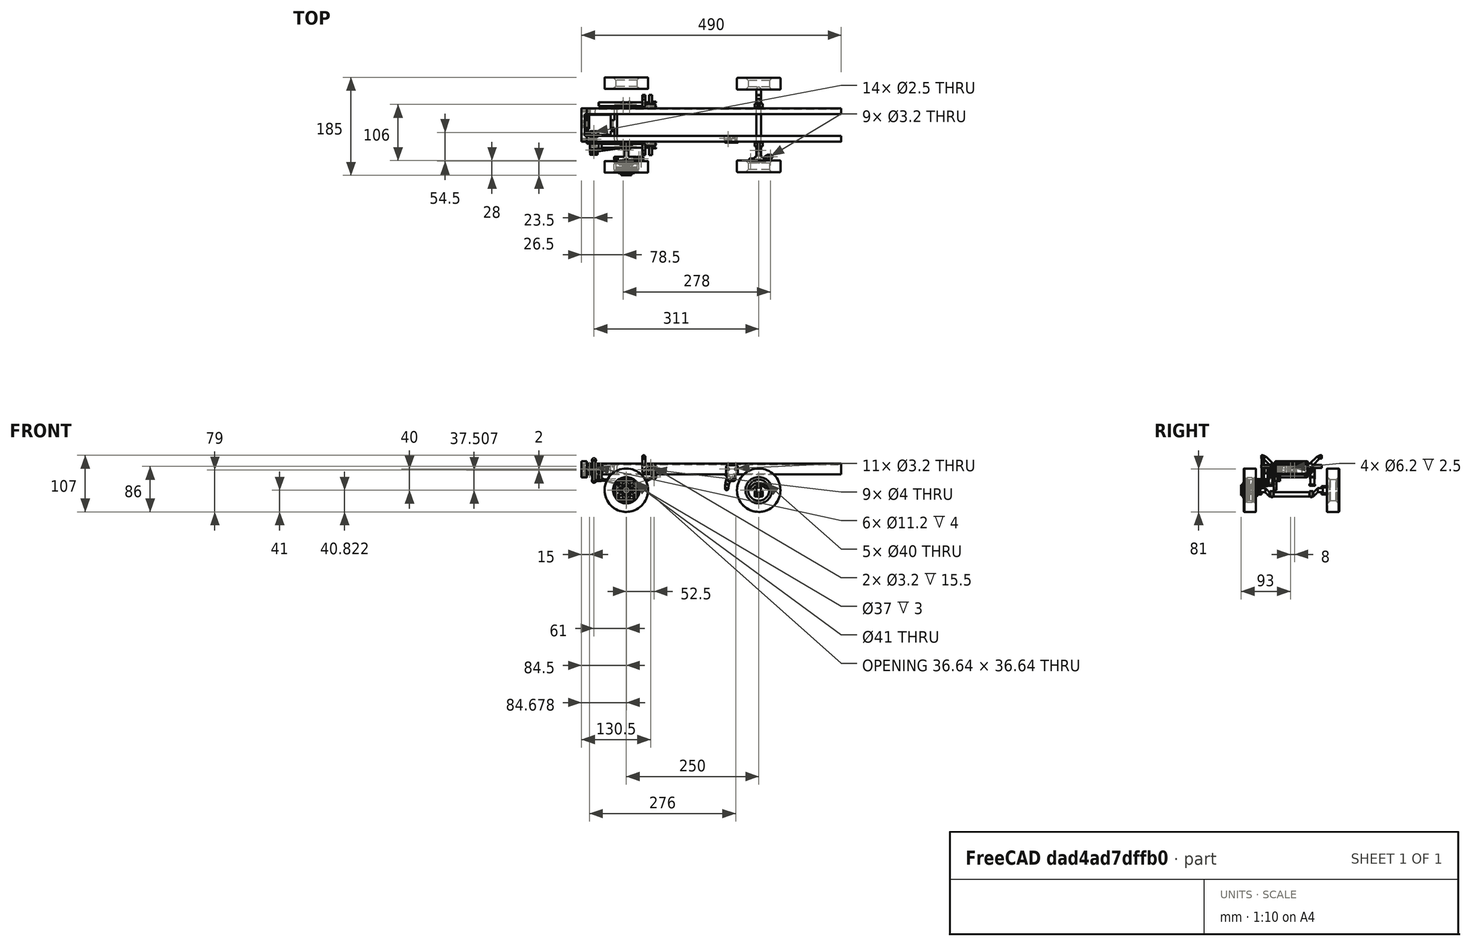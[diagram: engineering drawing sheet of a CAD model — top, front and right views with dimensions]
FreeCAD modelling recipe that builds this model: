
FCSTD DOCUMENT  (FreeCAD 0.16R6348 (Git))
Label: steering-linkage
License: All rights reserved
LicenseURL: http://en.wikipedia.org/wiki/All_rights_reserved
objects: Part::Cylinder×278, Part::Cut×158, Part::MultiFuse×147, Part::Box×113, Part::Fillet×39, Part::Chamfer×25, Part::Feature×10, Part::Mirroring×8, Part::Extrusion×5, App::DocumentObjectGroup×4, Part::Cone×3, Part::Loft×2
note: 788 computed .brp shape members not serialized (recipe doc carries the construction recipe); baked Part::Feature solids carry a one-line shape summary decoded from their .brp

FEATURE [Part::Box] Box416  label="Cube641"
  Height = 20
  Length = 480
  Placement = pos=(0,0,-92) rot=(0,0,1;0rad)
  Width = 11
FEATURE [Part::Box] Box417  label="Cube642"
  Height = 17
  Length = 480
  Placement = pos=(0,1.5,-90.5) rot=(0,0,1;0rad)
  Width = 10
FEATURE [Part::Cut] Cut429  label="Cut768"
  Base = -> Box416
  Tool = -> Box417
FEATURE [Part::Fillet] Fillet268
  Base = -> Cut429
  Edges = 2 edges r=3: [Edge11,Edge23]
  Placement = pos=(0,-1.5,0) rot=(0,0,1;0rad)
FEATURE [Part::Box] Box418  label="Cube643"
  Height = 20
  Length = 480
  Placement = pos=(0,0,-92) rot=(0,0,1;0rad)
  Width = 11
FEATURE [Part::Box] Box419  label="Cube644"
  Height = 17
  Length = 480
  Placement = pos=(0,1.5,-90.5) rot=(0,0,1;0rad)
  Width = 10
FEATURE [Part::Cut] Cut430  label="Cut769"
  Base = -> Box418
  Tool = -> Box419
FEATURE [Part::Fillet] Fillet269
  Base = -> Cut430
  Edges = 2 edges r=3: [Edge11,Edge23]
FEATURE [Part::Mirroring] Part__Mirroring036  label="Fillet269 (Mirror #29)"
  Base = (0,0,0)
  Normal = (0,1,0)
  Placement = pos=(0,61.5,0) rot=(0,0,1;0rad)
  Source = -> Fillet269
FEATURE [Part::MultiFuse] Fusion231  label="frame-00"
  Placement = pos=(23.5,55,71) rot=(0,0,1;0rad)
  Shapes = -> [Part__Mirroring036,Fillet268]
FEATURE [Part::MultiFuse] Fusion498
FEATURE [Part::Cut] Cut607
FEATURE [Part::Cut] Cut610  label="Cut880"
  Base = -> Cut607
FEATURE [Part::MultiFuse] Fusion500  label="central-axle"
  Shapes = -> [Cut610,Fusion498]
FEATURE [Part::Cylinder] Cylinder276
  Angle = 360
  Height = 22
  Placement = pos=(0,0,0) rot=(1,0,0;1.5708rad)
  Radius = 41
FEATURE [Part::Cylinder] Cylinder277
  Angle = 360
  Height = 22
  Placement = pos=(0,0,0) rot=(1,0,0;1.5708rad)
  Radius = 20
FEATURE [Part::Cut] Cut421  label="Cut764"
  Base = -> Cylinder276
  Tool = -> Cylinder277
FEATURE [Part::Fillet] Fillet260  label="wheel-000"
  Base = -> Cut421
  Edges = 2 edges r=1: [Edge1,Edge3]
  Placement = pos=(0,17,0) rot=(0,0,1;0rad)
FEATURE [Part::Cylinder] Cylinder278
  Angle = 360
  Height = 22
  Placement = pos=(0,0,0) rot=(1,0,0;1.5708rad)
  Radius = 41
FEATURE [Part::Cylinder] Cylinder279
  Angle = 360
  Height = 22
  Placement = pos=(0,0,0) rot=(1,0,0;1.5708rad)
  Radius = 20
FEATURE [Part::Cut] Cut422  label="Cut765"
  Base = -> Cylinder278
  Tool = -> Cylinder279
FEATURE [Part::Fillet] Fillet261  label="wheel-001"
  Base = -> Cut422
  Edges = 2 edges r=1: [Edge1,Edge3]
  Placement = pos=(0,175,0) rot=(0,0,1;0rad)
FEATURE [Part::Cylinder] Cylinder288
  Angle = 360
  Height = 22
  Placement = pos=(0,0,0) rot=(1,0,0;1.5708rad)
  Radius = 41
FEATURE [Part::Cylinder] Cylinder289
  Angle = 360
  Height = 22
  Placement = pos=(0,0,0) rot=(1,0,0;1.5708rad)
  Radius = 41
FEATURE [Part::Cylinder] Cylinder290
  Angle = 360
  Height = 22
  Placement = pos=(0,0,0) rot=(1,0,0;1.5708rad)
  Radius = 20
FEATURE [Part::Cut] Cut427  label="Cut766"
  Base = -> Cylinder289
  Tool = -> Cylinder290
FEATURE [Part::Fillet] Fillet267  label="wheel-007"
  Base = -> Cut427
  Edges = 2 edges r=1: [Edge1,Edge3]
  Placement = pos=(0,174,0) rot=(0,0,1;0rad)
FEATURE [Part::Cylinder] Cylinder291
  Angle = 360
  Height = 22
  Placement = pos=(0,0,0) rot=(1,0,0;1.5708rad)
  Radius = 20
FEATURE [Part::Cut] Cut428  label="Cut767"
  Base = -> Cylinder288
  Tool = -> Cylinder291
FEATURE [Part::Fillet] Fillet266  label="wheel-006"
  Base = -> Cut428
  Edges = 2 edges r=1: [Edge1,Edge3]
  Placement = pos=(0,18,0) rot=(0,0,1;0rad)
FEATURE [Part::MultiFuse] Fusion244
  Placement = pos=(348,0,-51) rot=(0,0,1;0rad)
  Shapes = -> [Fillet266,Fillet267]
FEATURE [Part::Chamfer] Chamfer056  label="whees-middle"
  Base = -> Fusion244
  Edges = 4 edges r=5: [Edge8,Edge9,Edge18,Edge19]
FEATURE [Part::MultiFuse] Fusion245
  Placement = pos=(98,0,-51) rot=(0,0,1;0rad)
  Shapes = -> [Fillet260,Fillet261]
FEATURE [Part::Chamfer] Chamfer057  label="whels-front"
  Base = -> Fusion245
  Edges = 4 edges r=5: [Edge8,Edge9,Edge18,Edge19]
FEATURE [Part::Cylinder] Cylinder640  label="Cylinder722"
  Angle = 360
  Height = 7
  Placement = pos=(60,105,0) rot=(0,0,1;4.18879rad)
  Radius = 105
FEATURE [Part::Cylinder] Cylinder641  label="Cylinder723"
  Angle = 360
  Height = 7
  Placement = pos=(60,105,0) rot=(0,0,1;4.10152rad)
  Radius = 103
FEATURE [Part::Cut] Cut109  label="leafspring-rear-left"
  Base = -> Cylinder640
  Placement = pos=(440,4,-64) rot=(1,0,0;1.5708rad)
  Tool = -> Cylinder641
FEATURE [Part::Cylinder] Cylinder642  label="Cylinder724"
  Angle = 360
  Height = 7
  Placement = pos=(60,105,0) rot=(0,0,1;4.18879rad)
  Radius = 105
FEATURE [Part::Cylinder] Cylinder643  label="Cylinder642"
  Angle = 360
  Height = 7
  Placement = pos=(60,105,0) rot=(0,0,1;4.10152rad)
  Radius = 103
FEATURE [Part::Cut] Cut110  label="leafspring-rear-right"
  Base = -> Cylinder642
  Placement = pos=(440,83,-64) rot=(1,0,0;1.5708rad)
  Tool = -> Cylinder643
FEATURE [Part::MultiFuse] Fusion091  label="leafsprings-front"
  Placement = pos=(-402,45,23) rot=(0,0,1;0rad)
  Shapes = -> [Cut109,Cut110]
FEATURE [Part::Cylinder] Cylinder654  label="Cylinder731"
  Angle = 360
  Height = 10
  Placement = pos=(0,0,12.7) rot=(1,0,0;1.5708rad)
  Radius = 2
FEATURE [Part::Cylinder] Cylinder655  label="Cylinder732"
  Angle = 360
  Height = 10
  Placement = pos=(0,0,0) rot=(1,0,0;1.5708rad)
  Radius = 2
FEATURE [Part::Box] Box439  label="Cube658"
  Height = 20
  Length = 8
  Placement = pos=(-4,-1,-3.5) rot=(0,0,1;0rad)
  Width = 1
FEATURE [Part::Fillet] Fillet320
  Base = -> Box439
  Edges = 4 edges r=2.99: [Edge2,Edge4,Edge6,Edge8]
FEATURE [Part::MultiFuse] Fusion437
  Shapes = -> [Cylinder654,Cylinder655]
FEATURE [Part::Cut] Cut559  label="Cut849"
  Base = -> Fillet320
  Placement = pos=(150,42,-27) rot=(0,-1,0;0.174533rad)
  Tool = -> Fusion437
FEATURE [Part::Cylinder] Cylinder656  label="Cylinder733"
  Angle = 360
  Height = 10
  Placement = pos=(0,0,12.7) rot=(1,0,0;1.5708rad)
  Radius = 2
FEATURE [Part::Cylinder] Cylinder657  label="Cylinder734"
  Angle = 360
  Height = 10
  Placement = pos=(0,0,0) rot=(1,0,0;1.5708rad)
  Radius = 2
FEATURE [Part::MultiFuse] Fusion438
  Shapes = -> [Cylinder656,Cylinder657]
FEATURE [Part::Box] Box440  label="Cube659"
  Height = 20
  Length = 8
  Placement = pos=(-4,-1,-3.5) rot=(0,0,1;0rad)
  Width = 1
FEATURE [Part::Fillet] Fillet321
  Base = -> Box440
  Edges = 4 edges r=2.99: [Edge2,Edge4,Edge6,Edge8]
FEATURE [Part::Cut] Cut560  label="Cut850"
  Base = -> Fillet321
  Placement = pos=(150,50,-27) rot=(0,-1,0;0.174533rad)
  Tool = -> Fusion438
FEATURE [Part::MultiFuse] Fusion439  label="leafspring-bisquits-front-left"
  Placement = pos=(0.5,0,1) rot=(0,0,1;0rad)
  Shapes = -> [Cut559,Cut560]
FEATURE [Part::Cylinder] Cylinder658  label="Cylinder768"
  Angle = 360
  Height = 10
  Placement = pos=(0,0,12.7) rot=(1,0,0;1.5708rad)
  Radius = 2
FEATURE [Part::Cylinder] Cylinder659  label="Cylinder712"
  Angle = 360
  Height = 10
  Placement = pos=(0,0,0) rot=(1,0,0;1.5708rad)
  Radius = 2
FEATURE [Part::Box] Box441  label="Cube660"
  Height = 20
  Length = 8
  Placement = pos=(-4,-1,-3.5) rot=(0,0,1;0rad)
  Width = 1
FEATURE [Part::Fillet] Fillet322
  Base = -> Box441
  Edges = 4 edges r=2.99: [Edge2,Edge4,Edge6,Edge8]
FEATURE [Part::MultiFuse] Fusion441
  Shapes = -> [Cylinder658,Cylinder659]
FEATURE [Part::Cut] Cut561  label="Cut851"
  Base = -> Fillet322
  Placement = pos=(150,42,-27) rot=(0,-1,0;0.174533rad)
  Tool = -> Fusion441
FEATURE [Part::Cylinder] Cylinder660  label="Cylinder783"
  Angle = 360
  Height = 10
  Placement = pos=(0,0,12.7) rot=(1,0,0;1.5708rad)
  Radius = 2
FEATURE [Part::Cylinder] Cylinder661  label="Cylinder784"
  Angle = 360
  Height = 10
  Placement = pos=(0,0,0) rot=(1,0,0;1.5708rad)
  Radius = 2
FEATURE [Part::MultiFuse] Fusion442
  Shapes = -> [Cylinder660,Cylinder661]
FEATURE [Part::Box] Box442  label="Cube661"
  Height = 20
  Length = 8
  Placement = pos=(-4,-1,-3.5) rot=(0,0,1;0rad)
  Width = 1
FEATURE [Part::Fillet] Fillet323
  Base = -> Box442
  Edges = 4 edges r=2.99: [Edge2,Edge4,Edge6,Edge8]
FEATURE [Part::Cut] Cut562  label="Cut852"
  Base = -> Fillet323
  Placement = pos=(150,50,-27) rot=(0,-1,0;0.174533rad)
  Tool = -> Fusion442
FEATURE [Part::MultiFuse] Fusion440  label="leafspring-bisquits-front-right"
  Placement = pos=(0.5,79,1) rot=(0,0,1;0rad)
  Shapes = -> [Cut561,Cut562]
FEATURE [Part::Cylinder] Cylinder681  label="Cylinder798"
  Angle = 360
  Height = 4
  Radius = 4.5
FEATURE [Part::Cylinder] Cylinder001
  Angle = 360
  Height = 4
  Placement = pos=(12,0,0) rot=(0,0,1;0rad)
  Radius = 4.5
FEATURE [Part::Box] Box453
  Height = 1
  Length = 12
  Placement = pos=(0,-4,0) rot=(0,0,1;0rad)
  Width = 8
FEATURE [Part::MultiFuse] Fusion453
  Shapes = -> [Box453,Cylinder001,Cylinder681]
FEATURE [Part::Box] Box454
  Height = 4
  Length = 12
  Placement = pos=(0,-4,0) rot=(0,0,1;0rad)
  Width = 1
FEATURE [Part::Box] Box455
  Height = 4
  Length = 12
  Placement = pos=(0,3,0) rot=(0,0,1;0rad)
  Width = 1
FEATURE [Part::Box] Box456
  Height = 1
  Length = 12
  Placement = pos=(0,3.5,3) rot=(0,0,1;0rad)
  Width = 0.5
FEATURE [Part::MultiFuse] Fusion001
  Shapes = -> [Fusion453,Box455,Box454]
FEATURE [Part::Box] Box004
  Height = 1
  Length = 12
  Placement = pos=(0,-4,3) rot=(0,0,1;0rad)
  Width = 0.5
FEATURE [Part::MultiFuse] Fusion002
  Shapes = -> [Fusion001,Box456,Box004]
FEATURE [Part::Cylinder] Cylinder002
  Angle = 360
  Height = 4
  Radius = 1.5
FEATURE [Part::Box] Box005
  Height = 10
  Length = 10
  Placement = pos=(-5,0,0) rot=(0,0,1;0rad)
  Width = 10
FEATURE [Part::Cut] Cut571  label="Cut859"
  Base = -> Cylinder002
  Placement = pos=(0,-4,0) rot=(0,0,1;0rad)
  Tool = -> Box005
FEATURE [Part::Cylinder] Cylinder003
  Angle = 360
  Height = 4
  Radius = 1.5
FEATURE [Part::Box] Box006
  Height = 10
  Length = 10
  Placement = pos=(-5,0,0) rot=(0,0,1;0rad)
  Width = 10
FEATURE [Part::Cut] Cut572  label="Cut860"
  Base = -> Cylinder003
  Placement = pos=(12,-4,0) rot=(0,0,1;0rad)
  Tool = -> Box006
FEATURE [Part::Cylinder] Cylinder682  label="Cylinder799"
  Angle = 360
  Height = 4
  Radius = 1.5
FEATURE [Part::Box] Box007
  Height = 10
  Length = 10
  Placement = pos=(-5,0,0) rot=(0,0,1;0rad)
  Width = 10
FEATURE [Part::Cut] Cut002
  Base = -> Cylinder682
  Placement = pos=(0,4,0) rot=(0,0,1;3.14159rad)
  Tool = -> Box007
FEATURE [Part::Cylinder] Cylinder005
  Angle = 360
  Height = 4
  Radius = 1.5
FEATURE [Part::Box] Box008
  Height = 10
  Length = 10
  Placement = pos=(-5,0,0) rot=(0,0,1;0rad)
  Width = 10
FEATURE [Part::Cut] Cut003
  Base = -> Cylinder005
  Placement = pos=(12,4,0) rot=(0,0,1;3.14159rad)
  Tool = -> Box008
FEATURE [Part::MultiFuse] Fusion003
  Shapes = -> [Fusion002,Cut003,Cut002,Cut572,Cut571]
FEATURE [Part::Cylinder] Cylinder006
  Angle = 360
  Height = 10
  Radius = 1.6
FEATURE [Part::Cylinder] Cylinder007
  Angle = 360
  Height = 10
  Placement = pos=(12,0,0) rot=(0,0,1;0rad)
  Radius = 1.6
FEATURE [Part::MultiFuse] Fusion004
  Shapes = -> [Cylinder007,Cylinder006]
FEATURE [Part::Cut] Cut004
  Base = -> Fusion003
  Tool = -> Fusion004
FEATURE [Part::Cylinder] Cylinder008
  Angle = 360
  Height = 7
  Placement = pos=(6,3.5,153) rot=(1,0,0;1.5708rad)
  Radius = 150
FEATURE [Part::Cut] Cut005
  Base = -> Cut004
  Tool = -> Cylinder008
FEATURE [Part::Box] Box457
  Height = 3
  Length = 6
  Placement = pos=(3,-3.5,1) rot=(0,0,1;0rad)
  Width = 7
FEATURE [Part::Cut] Cut006
  Base = -> Cut005
  Tool = -> Box457
FEATURE [Part::Box] Box015
  Height = 1.5
  Length = 26
  Placement = pos=(-6,-6,0) rot=(0,0,1;0rad)
  Width = 13
FEATURE [Part::Cut] Cut012
  Base = -> Cut006
  Placement = pos=(0,0,-1.5) rot=(0,0,1;0rad)
  Tool = -> Box015
FEATURE [Part::Box] Box016
  Height = 1
  Length = 8
  Placement = pos=(2,-4,0) rot=(0,0,1;0rad)
  Width = 8
FEATURE [Part::MultiFuse] Fusion008  label="leafspring-spacer-front-left"
  Placement = pos=(92,45,-42.5) rot=(0,0,1;0rad)
  Shapes = -> [Cut012,Box016]
FEATURE [Part::Cylinder] Cylinder683  label="Cylinder800"
  Angle = 360
  Height = 4
  Radius = 4.5
FEATURE [Part::Cylinder] Cylinder684  label="Cylinder801"
  Angle = 360
  Height = 4
  Placement = pos=(12,0,0) rot=(0,0,1;0rad)
  Radius = 4.5
FEATURE [Part::Box] Box458
  Height = 1
  Length = 12
  Placement = pos=(0,-4,0) rot=(0,0,1;0rad)
  Width = 8
FEATURE [Part::MultiFuse] Fusion454
  Shapes = -> [Box458,Cylinder684,Cylinder683]
FEATURE [Part::Box] Box459
  Height = 4
  Length = 12
  Placement = pos=(0,-4,0) rot=(0,0,1;0rad)
  Width = 1
FEATURE [Part::Box] Box460
  Height = 4
  Length = 12
  Placement = pos=(0,3,0) rot=(0,0,1;0rad)
  Width = 1
FEATURE [Part::Box] Box461
  Height = 1
  Length = 12
  Placement = pos=(0,3.5,3) rot=(0,0,1;0rad)
  Width = 0.5
FEATURE [Part::MultiFuse] Fusion455
  Shapes = -> [Fusion454,Box460,Box459]
FEATURE [Part::Box] Box462
  Height = 1
  Length = 12
  Placement = pos=(0,-4,3) rot=(0,0,1;0rad)
  Width = 0.5
FEATURE [Part::MultiFuse] Fusion456
  Shapes = -> [Fusion455,Box461,Box462]
FEATURE [Part::Cylinder] Cylinder685  label="Cylinder802"
  Angle = 360
  Height = 4
  Radius = 1.5
FEATURE [Part::Box] Box463
  Height = 10
  Length = 10
  Placement = pos=(-5,0,0) rot=(0,0,1;0rad)
  Width = 10
FEATURE [Part::Cut] Cut573  label="Cut861"
  Base = -> Cylinder685
  Placement = pos=(0,-4,0) rot=(0,0,1;0rad)
  Tool = -> Box463
FEATURE [Part::Cylinder] Cylinder686  label="Cylinder879"
  Angle = 360
  Height = 4
  Radius = 1.5
FEATURE [Part::Box] Box464
  Height = 10
  Length = 10
  Placement = pos=(-5,0,0) rot=(0,0,1;0rad)
  Width = 10
FEATURE [Part::Cut] Cut574  label="Cut862"
  Base = -> Cylinder686
  Placement = pos=(12,-4,0) rot=(0,0,1;0rad)
  Tool = -> Box464
FEATURE [Part::Cylinder] Cylinder687  label="Cylinder804"
  Angle = 360
  Height = 4
  Radius = 1.5
FEATURE [Part::Box] Box465
  Height = 10
  Length = 10
  Placement = pos=(-5,0,0) rot=(0,0,1;0rad)
  Width = 10
FEATURE [Part::Cut] Cut575  label="Cut863"
  Base = -> Cylinder687
  Placement = pos=(0,4,0) rot=(0,0,1;3.14159rad)
  Tool = -> Box465
FEATURE [Part::Cylinder] Cylinder688  label="Cylinder865"
  Angle = 360
  Height = 4
  Radius = 1.5
FEATURE [Part::Box] Box466
  Height = 10
  Length = 10
  Placement = pos=(-5,0,0) rot=(0,0,1;0rad)
  Width = 10
FEATURE [Part::Cut] Cut576  label="Cut864"
  Base = -> Cylinder688
  Placement = pos=(12,4,0) rot=(0,0,1;3.14159rad)
  Tool = -> Box466
FEATURE [Part::MultiFuse] Fusion457
  Shapes = -> [Fusion456,Cut576,Cut575,Cut574,Cut573]
FEATURE [Part::Cylinder] Cylinder689  label="Cylinder908"
  Angle = 360
  Height = 10
  Radius = 1.6
FEATURE [Part::Cylinder] Cylinder690  label="Cylinder909"
  Angle = 360
  Height = 10
  Placement = pos=(12,0,0) rot=(0,0,1;0rad)
  Radius = 1.6
FEATURE [Part::MultiFuse] Fusion458
  Shapes = -> [Cylinder690,Cylinder689]
FEATURE [Part::Cut] Cut577  label="Cut865"
  Base = -> Fusion457
  Tool = -> Fusion458
FEATURE [Part::Cylinder] Cylinder691  label="Cylinder910"
  Angle = 360
  Height = 7
  Placement = pos=(6,3.5,153) rot=(1,0,0;1.5708rad)
  Radius = 150
FEATURE [Part::Cut] Cut578  label="Cut866"
  Base = -> Cut577
  Tool = -> Cylinder691
FEATURE [Part::Box] Box467
  Height = 3
  Length = 6
  Placement = pos=(3,-3.5,1) rot=(0,0,1;0rad)
  Width = 7
FEATURE [Part::Cut] Cut579  label="Cut867"
  Base = -> Cut578
  Tool = -> Box467
FEATURE [Part::Box] Box468
  Height = 1.5
  Length = 26
  Placement = pos=(-6,-6,0) rot=(0,0,1;0rad)
  Width = 13
FEATURE [Part::Cut] Cut580  label="Cut868"
  Base = -> Cut579
  Placement = pos=(0,0,-1.5) rot=(0,0,1;0rad)
  Tool = -> Box468
FEATURE [Part::Box] Box469
  Height = 1
  Length = 8
  Placement = pos=(2,-4,0) rot=(0,0,1;0rad)
  Width = 8
FEATURE [Part::MultiFuse] Fusion459  label="leafspring-spacer-front-right"
  Placement = pos=(92,124,-42.5) rot=(0,0,1;0rad)
  Shapes = -> [Cut580,Box469]
FEATURE [Part::Box] Box021
  Height = 1
  Length = 12
  Placement = pos=(0,-21.75,0) rot=(0,0,1;0rad)
  Width = 7.5
FEATURE [Part::Cylinder] Cylinder016
  Angle = 360
  Height = 1
  Placement = pos=(12,-18,0) rot=(0,0,1;0rad)
  Radius = 4.75
FEATURE [Part::Cylinder] Cylinder017
  Angle = 360
  Height = 1
  Placement = pos=(0,-18,0) rot=(0,0,1;0rad)
  Radius = 4.75
FEATURE [Part::Box] Box022
  Height = 300
  Length = 317
  Placement = pos=(-150,-22,0) rot=(0,0,1;0rad)
  Width = 10
FEATURE [Part::Cylinder] Cylinder018
  Angle = 360
  Height = 7.5
  Placement = pos=(6,-14.25,49.2) rot=(1,0,0;1.5708rad)
  Radius = 50
FEATURE [Part::Cut] Cut018
  Base = -> Cylinder018
  Tool = -> Box022
FEATURE [Part::MultiFuse] Fusion014
  Shapes = -> [Box021,Cut018,Cylinder017,Cylinder016]
FEATURE [Part::Cylinder] Cylinder019
  Angle = 360
  Height = 7.5
  Placement = pos=(6,-14.25,49.2) rot=(1,0,0;1.5708rad)
  Radius = 51
FEATURE [Part::Cylinder] Cylinder020
  Angle = 360
  Height = 7.5
  Placement = pos=(6,-14.25,49.2) rot=(1,0,0;1.5708rad)
  Radius = 50
FEATURE [Part::Cut] Cut019
  Base = -> Cylinder019
  Tool = -> Cylinder020
FEATURE [Part::Cut] Cut020
  Base = -> Fusion014
  Tool = -> Cut019
FEATURE [Part::Cylinder] Cylinder021
  Angle = 360
  Height = 10
  Placement = pos=(12,-18,-9.2) rot=(0,0,1;0rad)
  Radius = 1.6
FEATURE [Part::Cylinder] Cylinder022
  Angle = 360
  Height = 10
  Placement = pos=(0,-18,-9.2) rot=(0,0,1;0rad)
  Radius = 1.6
FEATURE [Part::MultiFuse] Fusion015
  Placement = pos=(0,0,5) rot=(0,0,1;0rad)
  Shapes = -> [Cylinder021,Cylinder022]
FEATURE [Part::Cut] Cut021  label="leafspring-spacer-upper-front-left"
  Base = -> Cut020
  Placement = pos=(92,63,-38) rot=(0,0,1;0rad)
  Tool = -> Fusion015
FEATURE [Part::Box] Box485  label="Cube687"
  Height = 17
  Length = 25
  Placement = pos=(128,45.5,-18) rot=(0,0,1;0rad)
  Width = 8
FEATURE [Part::Cylinder] Cylinder735  label="Cylinder911"
  Angle = 360
  Height = 25.5
  Placement = pos=(144,53.5,-6) rot=(1,0,0;1.5708rad)
  Radius = 3
FEATURE [Part::Cylinder] Cylinder736  label="Cylinder912"
  Angle = 360
  Height = 23
  Placement = pos=(131,51,-6) rot=(1,0,0;0.785398rad)
  Radius = 3
FEATURE [Part::Feature] Face036
  shape: bbox 7.785 x 2e-07 x 7.712 mm, 1 faces, 0 solids (baked)
FEATURE [Part::Feature] Face037
  shape: bbox 7.318 x 4.987 x 4.987 mm, 1 faces, 0 solids (baked)
FEATURE [Part::Loft] Loft014
  Closed = false
  Ruled = true
  Sections = -> [Face036,Face037]
  Solid = true
FEATURE [Part::Cylinder] Cylinder737  label="Cylinder902"
  Angle = 360
  Height = 3
  Placement = pos=(131,31,12) rot=(1,0,0;1.5708rad)
  Radius = 3
FEATURE [Part::MultiFuse] Fusion480
  Shapes = -> [Loft014,Cylinder737]
FEATURE [Part::Cylinder] Cylinder738  label="Cylinder913"
  Angle = 360
  Height = 5
  Placement = pos=(131,33,12) rot=(1,0,0;1.5708rad)
  Radius = 1.6
FEATURE [Part::Cylinder] Cylinder739  label="Cylinder914"
  Angle = 360
  Height = 15.5
  Placement = pos=(144,43.5,-6) rot=(1,0,0;1.5708rad)
  Radius = 1.6
FEATURE [Part::MultiFuse] Fusion481
  Shapes = -> [Cylinder738,Cylinder739]
FEATURE [Part::Cylinder] Cylinder740  label="Cylinder915"
  Angle = 360
  Height = 15
  Placement = pos=(132,61.5,-16) rot=(1,0,0;1.5708rad)
  Radius = 1.6
FEATURE [Part::Cylinder] Cylinder741  label="Cylinder916"
  Angle = 360
  Height = 2.5
  Placement = pos=(132,49,-16) rot=(1,0,0;1.5708rad)
  Radius = 3
FEATURE [Part::MultiFuse] Fusion482
  Placement = pos=(4,-1.5,4) rot=(0,0,1;0rad)
  Shapes = -> [Cylinder740,Cylinder741]
FEATURE [Part::Box] Box488  label="Cube690"
  Height = 9.5
  Length = 10
  Placement = pos=(143,45.5,-18) rot=(0,0,1;0rad)
  Width = 5
FEATURE [Part::Fillet] Fillet337
  Base = -> Box488
  Edges = 1 edges r=4: [Edge2]
FEATURE [Part::Cylinder] Cylinder745  label="Cylinder890"
  Angle = 360
  Height = 3.5
  Placement = pos=(148.5,53.5,-13.5) rot=(1,0,0;1.5708rad)
  Radius = 3
FEATURE [Part::Cylinder] Cylinder746  label="Cylinder917"
  Angle = 360
  Height = 1.75
  Placement = pos=(498.5,51.75,-13.5) rot=(1,0,0;1.5708rad)
  Radius = 2.1
FEATURE [Part::Cylinder] Cylinder747  label="Cylinder892"
  Angle = 360
  Height = 3.5
  Placement = pos=(498.5,53.5,-13.5) rot=(1,0,0;1.5708rad)
  Radius = 1.5
FEATURE [Part::MultiFuse] Fusion484
  Placement = pos=(-350,0,0) rot=(0,0,1;0rad)
  Shapes = -> [Cylinder746,Cylinder747]
FEATURE [Part::Cylinder] Cylinder748  label="Cylinder964"
  Angle = 360
  Height = 75
  Placement = pos=(121,50,-7) rot=(0,1,0;1.5708rad)
  Radius = 3
FEATURE [Part::Cut] Cut595  label="Cut874"
  Base = -> Box485
  Tool = -> Fillet337
FEATURE [Part::MultiFuse] Fusion485
  Shapes = -> [Cut595,Cylinder745]
FEATURE [Part::Cut] Cut596  label="Cut875"
  Base = -> Fusion485
  Tool = -> Fusion484
FEATURE [Part::MultiFuse] Fusion486
  Shapes = -> [Cut596,Fusion480,Cylinder736,Cylinder735]
FEATURE [Part::Cut] Cut597
  Base = -> Fusion486
  Tool = -> Fusion481
FEATURE [Part::Cut] Cut598  label="wing-support-left_"
  Base = -> Cut597
  Tool = -> Fusion482
FEATURE [Part::Box] Box489  label="Cube691"
  Height = 17
  Length = 25
  Placement = pos=(128,45.5,-18) rot=(0,0,1;0rad)
  Width = 8
FEATURE [Part::Cylinder] Cylinder749  label="Cylinder965"
  Angle = 360
  Height = 25.5
  Placement = pos=(144,53.5,-6) rot=(1,0,0;1.5708rad)
  Radius = 3
FEATURE [Part::Cylinder] Cylinder750  label="Cylinder966"
  Angle = 360
  Height = 23
  Placement = pos=(131,51,-6) rot=(1,0,0;0.785398rad)
  Radius = 3
FEATURE [Part::Feature] Face038
  shape: bbox 7.785 x 2e-07 x 7.712 mm, 1 faces, 0 solids (baked)
FEATURE [Part::Feature] Face039
  shape: bbox 7.318 x 4.987 x 4.987 mm, 1 faces, 0 solids (baked)
FEATURE [Part::Loft] Loft015
  Closed = false
  Ruled = true
  Sections = -> [Face038,Face039]
  Solid = true
FEATURE [Part::Cylinder] Cylinder751  label="Cylinder967"
  Angle = 360
  Height = 3
  Placement = pos=(131,31,12) rot=(1,0,0;1.5708rad)
  Radius = 3
FEATURE [Part::MultiFuse] Fusion487
  Shapes = -> [Loft015,Cylinder751]
FEATURE [Part::Cylinder] Cylinder752  label="Cylinder968"
  Angle = 360
  Height = 5
  Placement = pos=(131,33,12) rot=(1,0,0;1.5708rad)
  Radius = 1.6
FEATURE [Part::Cylinder] Cylinder753  label="Cylinder969"
  Angle = 360
  Height = 15.5
  Placement = pos=(144,43.5,-6) rot=(1,0,0;1.5708rad)
  Radius = 1.6
FEATURE [Part::MultiFuse] Fusion488
  Shapes = -> [Cylinder752,Cylinder753]
FEATURE [Part::Cylinder] Cylinder754  label="Cylinder970"
  Angle = 360
  Height = 15
  Placement = pos=(132,61.5,-16) rot=(1,0,0;1.5708rad)
  Radius = 1.6
FEATURE [Part::Cylinder] Cylinder755  label="Cylinder971"
  Angle = 360
  Height = 2.5
  Placement = pos=(132,49,-16) rot=(1,0,0;1.5708rad)
  Radius = 3
FEATURE [Part::MultiFuse] Fusion489
  Placement = pos=(4,-1.5,4) rot=(0,0,1;0rad)
  Shapes = -> [Cylinder754,Cylinder755]
FEATURE [Part::Box] Box490  label="Cube692"
  Height = 9.5
  Length = 10
  Placement = pos=(143,45.5,-18) rot=(0,0,1;0rad)
  Width = 5
FEATURE [Part::Fillet] Fillet338
  Base = -> Box490
  Edges = 1 edges r=4: [Edge2]
FEATURE [Part::Cylinder] Cylinder756  label="Cylinder972"
  Angle = 360
  Height = 3.5
  Placement = pos=(148.5,53.5,-13.5) rot=(1,0,0;1.5708rad)
  Radius = 3
FEATURE [Part::Cylinder] Cylinder757  label="Cylinder973"
  Angle = 360
  Height = 1.75
  Placement = pos=(498.5,51.75,-13.5) rot=(1,0,0;1.5708rad)
  Radius = 2.1
FEATURE [Part::Cylinder] Cylinder758  label="Cylinder941"
  Angle = 360
  Height = 3.5
  Placement = pos=(498.5,53.5,-13.5) rot=(1,0,0;1.5708rad)
  Radius = 1.5
FEATURE [Part::MultiFuse] Fusion490
  Placement = pos=(-350,0,0) rot=(0,0,1;0rad)
  Shapes = -> [Cylinder757,Cylinder758]
FEATURE [Part::Cut] Cut602  label="Cut877"
  Base = -> Box489
  Tool = -> Fillet338
FEATURE [Part::MultiFuse] Fusion492
  Shapes = -> [Cut602,Cylinder756]
FEATURE [Part::Cut] Cut600  label="Cut876"
  Base = -> Fusion492
  Tool = -> Fusion490
FEATURE [Part::MultiFuse] Fusion491
  Shapes = -> [Cut600,Fusion487,Cylinder750,Cylinder749]
FEATURE [Part::Cut] Cut601
  Base = -> Fusion491
  Tool = -> Fusion488
FEATURE [Part::Cut] Cut599  label="wing-support-left001"
  Base = -> Cut601
  Tool = -> Fusion489
FEATURE [Part::Mirroring] Part__Mirroring095  label="wing-support-right"
  Base = (0,0,0)
  Normal = (0,1,0)
  Placement = pos=(0,170,0) rot=(0,0,1;0rad)
  Source = -> Cut599
FEATURE [Part::Cut] Cut603  label="wing-support-left"
  Base = -> Cut598
  Tool = -> Cylinder748
FEATURE [Part::Cylinder] Cylinder692  label="Cylinder942"
  Angle = 360
  Height = 10
  Placement = pos=(3,60,10) rot=(1,0,0;1.5708rad)
  Radius = 1.2
FEATURE [Part::Cylinder] Cylinder693  label="Cylinder943"
  Angle = 360
  Height = 10
  Placement = pos=(3,10,10) rot=(1,0,0;1.5708rad)
  Radius = 1.2
FEATURE [Part::Box] Box472  label="Cube674"
  Height = 17
  Length = 16
  Placement = pos=(-2,0,1.5) rot=(0,0,1;0rad)
  Width = 60
FEATURE [Part::Box] Box473  label="Cube675"
  Height = 25.5
  Length = 10
  Placement = pos=(-12,0,-5) rot=(0,0,1;0rad)
  Width = 63
FEATURE [Part::Cylinder] Cylinder694  label="Cylinder944"
  Angle = 360
  Height = 11
  Placement = pos=(-2,66.5,-1) rot=(0,1,0;1.5708rad)
  Radius = 1.25
FEATURE [Part::Cylinder] Cylinder695  label="Cylinder974"
  Angle = 360
  Height = 11
  Placement = pos=(-2,13.5,-1) rot=(0,1,0;1.5708rad)
  Radius = 1.25
FEATURE [Part::Cylinder] Cylinder696  label="Cylinder975"
  Angle = 360
  Height = 15
  Placement = pos=(-2,57,15) rot=(0,1,0;1.5708rad)
  Radius = 1.25
FEATURE [Part::Cylinder] Cylinder697  label="Cylinder976"
  Angle = 360
  Height = 15
  Placement = pos=(-2,23,15) rot=(0,1,0;1.5708rad)
  Radius = 1.25
FEATURE [Part::MultiFuse] Fusion460
  Placement = pos=(-10,-10,1) rot=(0,0,1;0rad)
  Shapes = -> [Cylinder694,Cylinder697,Cylinder695,Cylinder696]
FEATURE [Part::Fillet] Fillet332
  Base = -> Box473
  Edges = 4 edges r=3: [Edge9,Edge10,Edge11,Edge12]
  Placement = pos=(25.5,53.5,-21.5) rot=(0,0,1;0rad)
FEATURE [Part::Fillet] Fillet333
  Base = -> Box472
  Edges = 4 edges r=3: [Edge9,Edge10,Edge11,Edge12]
  Placement = pos=(25.5,55,-21) rot=(0,0,1;0rad)
FEATURE [Part::MultiFuse] Fusion462
  Placement = pos=(0,0,2) rot=(0,0,1;0rad)
  Shapes = -> [Cylinder692,Cylinder693]
FEATURE [Part::MultiFuse] Fusion463
  Placement = pos=(25.5,55,-23) rot=(0,0,1;0rad)
  Shapes = -> [Fusion460,Fusion462]
FEATURE [Part::MultiFuse] Fusion464
  Shapes = -> [Fillet332,Fillet333]
FEATURE [Part::Cut] Cut581  label="cross-member-front_00"
  Base = -> Fusion464
  Tool = -> Fusion463
FEATURE [Part::Cylinder] Cylinder770  label="Cylinder977"
  Angle = 360
  Height = 3
  Placement = pos=(0,0,1) rot=(0,0,1;0rad)
  Radius = 4
FEATURE [Part::Cylinder] Cylinder771  label="Cylinder978"
  Angle = 360
  Height = 3
  Placement = pos=(-37,7,3) rot=(0,0,1;0rad)
  Radius = 4
FEATURE [Part::Cylinder] Cylinder772  label="Cylinder979"
  Angle = 360
  Height = 4
  Placement = pos=(-15,0,8) rot=(0,0,1;0rad)
  Radius = 4.5
FEATURE [Part::Box] Box507  label="Cube021"
  Height = 4
  Length = 8
  Placement = pos=(-19,0,8) rot=(0,0,1;0rad)
  Width = 27
FEATURE [Part::Cylinder] Cylinder773  label="Cylinder980"
  Angle = 360
  Height = 4
  Placement = pos=(-15,27,8) rot=(0,0,1;0rad)
  Radius = 4
FEATURE [Part::Cylinder] Cylinder774  label="Cylinder981"
  Angle = 360
  Height = 2
  Placement = pos=(-15,0,8) rot=(0,0,1;0rad)
  Radius = 3.2
FEATURE [Part::Box] Box508  label="Cube022"
  Height = 4
  Length = 11
  Placement = pos=(-15,-4,8) rot=(0,0,1;0rad)
  Width = 8
FEATURE [Part::Box] Box023  label="Cube023"
  Height = 4
  Length = 6
  Placement = pos=(-37,3,8) rot=(0,0,1;0rad)
  Width = 8
FEATURE [Part::Box] Box024  label="Cube709"
  Height = 4
  Length = 15
  Placement = pos=(-36,5,8) rot=(0,0,-1;0.663225rad)
  Width = 8
FEATURE [Part::Box] Box025  label="Cube025"
  Height = 4
  Length = 9
  Placement = pos=(-24,-4,8) rot=(0,0,1;0rad)
  Width = 8
FEATURE [Part::Box] Box026  label="Cube026"
  Height = 4
  Length = 10
  Placement = pos=(-30,-14,8) rot=(0,0,1;0rad)
  Width = 10
FEATURE [Part::Box] Box027  label="Cube027"
  Height = 4
  Length = 10
  Placement = pos=(-35,11,8) rot=(0,0,1;0rad)
  Width = 10
FEATURE [Part::MultiFuse] Fusion507
  Shapes = -> [Box026,Box027]
FEATURE [Part::MultiFuse] Fusion017
  Shapes = -> [Box023,Box024,Box025]
FEATURE [Part::Cut] Cut609  label="Cut881"
  Base = -> Fusion017
  Tool = -> Fusion507
FEATURE [Part::Cylinder] Cylinder775  label="Cylinder982"
  Angle = 360
  Height = 10
  Radius = 1.6
FEATURE [Part::Cylinder] Cylinder776  label="Cylinder983"
  Angle = 360
  Height = 10
  Placement = pos=(-37,7,2) rot=(0,0,1;0rad)
  Radius = 1.6
FEATURE [Part::Box] Box028  label="Cube028"
  Height = 4
  Length = 14
  Placement = pos=(-15,-6,8) rot=(0,0,1;0.785398rad)
  Width = 14
FEATURE [Part::Box] Box029  label="Cube029"
  Height = 4
  Length = 10
  Placement = pos=(-20,-14,8) rot=(0,0,1;0rad)
  Width = 10
FEATURE [Part::Cut] Cut013
  Base = -> Box028
  Tool = -> Box029
FEATURE [Part::MultiFuse] Fusion508
  Shapes = -> [Box508,Box507,Cut013,Cut609,Cylinder773,Cylinder772]
FEATURE [Part::Cut] Cut014
  Base = -> Fusion508
  Tool = -> Cylinder774
FEATURE [Part::Box] Box032  label="Cube032"
  Height = 11
  Length = 10
  Placement = pos=(-10,-4,1) rot=(0,0,1;0rad)
  Width = 8
FEATURE [Part::Chamfer] Chamfer082
  Base = -> Box032
  Edges = 1 edges r=7: [Edge4]
FEATURE [Part::Chamfer] Chamfer083
  Base = -> Chamfer082
  Edges = 1 edges r=6: [Edge12]
FEATURE [Part::Chamfer] Chamfer084
  Base = -> Cut014
  Edges = 1 edges r=2: [Edge2]
FEATURE [Part::MultiFuse] Fusion020
  Shapes = -> [Chamfer084,Chamfer083]
FEATURE [Part::Cylinder] Cylinder024
  Angle = 360
  Height = 10
  Placement = pos=(0,0,4) rot=(0,0,1;0rad)
  Radius = 3.2
FEATURE [Part::Cut] Cut015
  Base = -> Fusion020
  Tool = -> Cylinder024
FEATURE [Part::Box] Box033  label="Cube033"
  Height = 8
  Length = 10
  Placement = pos=(-10.2,-1,0) rot=(0,0,1;0.785398rad)
  Width = 10
FEATURE [Part::Cut] Cut016
  Base = -> Cut015
  Tool = -> Box033
FEATURE [Part::MultiFuse] Fusion022
  Shapes = -> [Cylinder770,Cut016]
FEATURE [Part::Cylinder] Cylinder025
  Angle = 360
  Height = 10
  Placement = pos=(-15,27,4) rot=(0,0,1;0rad)
  Radius = 1.6
FEATURE [Part::MultiFuse] Fusion023
  Shapes = -> [Cylinder775,Cylinder025]
FEATURE [Part::Cut] Cut017
  Base = -> Fusion022
  Tool = -> Fusion023
FEATURE [Part::MultiFuse] Fusion024
  Shapes = -> [Box026,Box027]
FEATURE [Part::MultiFuse] Fusion025
  Shapes = -> [Box023,Box024,Box025]
FEATURE [Part::Cut] Cut611  label="Cut882"
  Base = -> Fusion025
  Placement = pos=(0,0,-4) rot=(0,0,1;0rad)
  Tool = -> Fusion024
FEATURE [Part::Box] Box034  label="Cube034"
  Height = 10
  Length = 10
  Placement = pos=(-23,-4,0) rot=(0,0,1;0rad)
  Width = 11
FEATURE [Part::Cut] Cut612  label="Cut883"
  Base = -> Cut611
  Tool = -> Box034
FEATURE [Part::Chamfer] Chamfer085
  Base = -> Cut612
  Edges = 1 edges r=3.99: [Edge20]
FEATURE [Part::Box] Box035  label="Cube035"
  Height = 10
  Length = 10
  Placement = pos=(-39,-2,8) rot=(0,0,1;0rad)
  Width = 15
FEATURE [Part::Cut] Cut613  label="Cut884"
  Base = -> Cut017
  Tool = -> Box035
FEATURE [Part::Chamfer] Chamfer086
  Base = -> Cut613
  Edges = 1 edges r=3.99: [Edge32]
FEATURE [Part::MultiFuse] Fusion026
  Shapes = -> [Chamfer085,Chamfer086]
FEATURE [Part::MultiFuse] Fusion027
  Shapes = -> [Cylinder771,Fusion026]
FEATURE [Part::Cylinder] Cylinder026
  Angle = 360
  Height = 10
  Placement = pos=(-37,7,6) rot=(0,0,1;0rad)
  Radius = 3.2
FEATURE [Part::Chamfer] Chamfer087
  Base = -> Fusion027
  Edges = 1 edges r=1: [Edge20]
FEATURE [Part::Cut] Cut614  label="Cut885"
  Base = -> Chamfer087
  Tool = -> Cylinder026
FEATURE [Part::Box] Box509  label="Cube036"
  Height = 1
  Length = 6
  Placement = pos=(-37,3,3) rot=(0,0,1;0rad)
  Width = 8
FEATURE [Part::MultiFuse] Fusion028
  Shapes = -> [Cut614,Box509]
FEATURE [Part::Chamfer] Chamfer088
  Base = -> Fusion028
  Edges = 1 edges r=0.99: [Edge51]
FEATURE [Part::Cut] Cut022
  Base = -> Chamfer088
  Tool = -> Cylinder776
FEATURE [Part::Chamfer] Chamfer089
  Base = -> Cut022
  Edges = 2 edges r=1: [Edge17,Edge50]
FEATURE [Part::Box] Box037  label="Cube037"
  Height = 10
  Length = 10
  Placement = pos=(-19,23,3) rot=(0,0,1;0rad)
  Width = 10
FEATURE [Part::Cut] Cut023
  Base = -> Chamfer089
  Tool = -> Box037
FEATURE [Part::Cylinder] Cylinder027
  Angle = 360
  Height = 4
  Placement = pos=(-15,23,8) rot=(0,0,1;0rad)
  Radius = 4
FEATURE [Part::MultiFuse] Fusion509
  Shapes = -> [Cut023,Cylinder027]
FEATURE [Part::Cylinder] Cylinder028
  Angle = 360
  Height = 4
  Placement = pos=(-15,23,8) rot=(0,0,1;0rad)
  Radius = 1.6
FEATURE [Part::Cut] Cut024
  Base = -> Fusion509
  Tool = -> Cylinder028
FEATURE [Part::Mirroring] Part__Mirroring096  label="Cut024 (Mirror #73)"
  Base = (0,0,0)
  Normal = (0,1,0)
  Placement = pos=(333,18,-51) rot=(0,0,1;3.14159rad)
  Source = -> Cut024
FEATURE [Part::Cylinder] Cylinder778  label="Cylinder984"
  Angle = 360
  Height = 5
  Placement = pos=(348,37,-43) rot=(0,0,1;0rad)
  Radius = 1.25
FEATURE [Part::Box] Box515  label="Cube715"
  Height = 20
  Length = 22
  Placement = pos=(290.5,51.5,-24) rot=(0,0,1;0rad)
  Width = 12
FEATURE [Part::Cylinder] Cylinder781  label="Cylinder985"
  Angle = 360
  Height = 5
  Placement = pos=(338.5,56.5,-46) rot=(1,0,0;1.5708rad)
  Radius = 50
FEATURE [Part::Box] Box516  label="Cube716"
  Height = 50
  Length = 20
  Placement = pos=(288.5,51.5,-46) rot=(0,0,1;0rad)
  Width = 5
FEATURE [Part::Box] Box517  label="Cube717"
  Height = 50
  Length = 20
  Placement = pos=(288.5,51.5,-51) rot=(0,0,1;0rad)
  Width = 5
FEATURE [Part::Cut] Cut617  label="Cut888"
  Base = -> Box516
  Tool = -> Cylinder781
FEATURE [Part::Cut] Cut618  label="Cut889"
  Base = -> Box517
  Tool = -> Cut617
FEATURE [Part::Cylinder] Cylinder782  label="Cylinder986"
  Angle = 360
  Height = 5
  Placement = pos=(334.5,56.5,-51) rot=(1,0,0;1.5708rad)
  Radius = 40
FEATURE [Part::Chamfer] Chamfer091
  Base = -> Box515
  Edges = 1 edges r=5: [Edge4]
FEATURE [Part::Chamfer] Chamfer092
  Base = -> Chamfer091
  Edges = 1 edges r=5: [Edge15]
FEATURE [Part::Box] Box519  label="Cube719"
  Height = 20
  Length = 22
  Placement = pos=(290.5,53.5,-21) rot=(0,0,1;0rad)
  Width = 12
FEATURE [Part::Fillet] Fillet341
  Base = -> Box519
  Edges = 1 edges r=3: [Edge9]
FEATURE [Part::Cut] Cut619  label="Cut890"
  Base = -> Cut618
  Tool = -> Cylinder782
FEATURE [Part::MultiFuse] Fusion510
  Shapes = -> [Chamfer092,Cut619]
FEATURE [Part::Fillet] Fillet342
  Base = -> Fusion510
  Edges = 8 edges r=2.99: [Edge2,Edge3,Edge8,Edge11,Edge16,Edge19,Edge24,Edge32]
FEATURE [Part::Fillet] Fillet343
  Base = -> Fillet342
  Edges = 1 edges r=4: [Edge51]
FEATURE [Part::Fillet] Fillet344
  Base = -> Fillet343
  Edges = 1 edges r=2: [Edge43]
FEATURE [Part::Cut] Cut620  label="Cut891"
  Base = -> Fillet344
  Tool = -> Fillet341
FEATURE [Part::Cylinder] Cylinder790
  Angle = 360
  Height = 6
  Placement = pos=(303.5,59,-30) rot=(1,0,0;1.5708rad)
  Radius = 5
FEATURE [Part::Box] Box521  label="Cube721"
  Height = 11
  Length = 10
  Placement = pos=(298,51.5,-34) rot=(0,0,1;0rad)
  Width = 12
FEATURE [Part::Fillet] Fillet348
  Base = -> Box521
  Edges = 1 edges r=4: [Edge8]
FEATURE [Part::Cylinder] Cylinder791
  Angle = 360
  Height = 13
  Placement = pos=(303.5,63.75,-30) rot=(1,0,0;1.5708rad)
  Radius = 1.25
FEATURE [Part::Cylinder] Cylinder792
  Angle = 360
  Height = 10
  Placement = pos=(291.5,60.75,-48) rot=(1,0,0;1.5708rad)
  Radius = 1.25
FEATURE [Part::Cylinder] Cylinder793
  Angle = 360
  Height = 10
  Placement = pos=(308.5,57.75,-11) rot=(1,0,0;1.5708rad)
  Radius = 1.6
FEATURE [Part::Cylinder] Cylinder794
  Angle = 360
  Height = 10
  Placement = pos=(294.5,57.75,-11) rot=(1,0,0;1.5708rad)
  Radius = 1.6
FEATURE [Part::Cylinder] Cylinder795
  Angle = 360
  Height = 10
  Placement = pos=(294.5,59.75,-25) rot=(0,0,1;0rad)
  Radius = 1.6
FEATURE [Part::Box] Box522  label="Cube722"
  Height = 3
  Length = 10
  Placement = pos=(287,56.5,-24) rot=(0,0,1;0rad)
  Width = 7
FEATURE [Part::Chamfer] Chamfer
  Base = -> Box522
  Edges = 1 edges r=2.99: [Edge4]
FEATURE [Part::Fillet] Fillet349
  Base = -> Chamfer
  Edges = 1 edges r=3: [Edge9]
FEATURE [Part::MultiFuse] Fusion514
  Shapes = -> [Cut620,Fillet349]
FEATURE [Part::MultiFuse] Fusion515
  Shapes = -> [Fillet348,Fusion514]
FEATURE [Part::MultiFuse] Fusion516
  Shapes = -> [Cylinder793,Cylinder791,Cylinder794,Cylinder795,Cylinder790,Cylinder792]
FEATURE [Part::Cut] Cut622
  Base = -> Fusion515
  Tool = -> Fusion516
FEATURE [Part::Cylinder] Cylinder796  label="Cylinder987"
  Angle = 360
  Height = 4
  Placement = pos=(348,37,-43) rot=(0,0,1;0rad)
  Radius = 4
FEATURE [Part::Fillet] Fillet350
  Base = -> Cut622
  Edges = 4 edges r=0.5: [Edge5,Edge36,Edge57,Edge64]
  Placement = pos=(-4,0,0) rot=(0,0,1;0rad)
FEATURE [Part::Cylinder] Cylinder803  label="Cylinder988"
  Angle = 360
  Height = 10
  Placement = pos=(288.5,55.5,-40) rot=(1,0,0;1.5708rad)
  Radius = 0.9
FEATURE [Part::Cylinder] Cylinder805  label="Cylinder989"
  Angle = 360
  Height = 10
  Placement = pos=(290.5,55.5,-33) rot=(1,0,0;1.5708rad)
  Radius = 0.9
FEATURE [Part::MultiFuse] Fusion521
  Shapes = -> [Cylinder805,Cylinder803]
FEATURE [Part::Box] Box526  label="Cube726"
  Height = 10
  Length = 10
  Placement = pos=(343,37,-46) rot=(0,0,1;0rad)
  Width = 10
FEATURE [Part::Cut] Cut630
  Base = -> Part__Mirroring096
  Tool = -> Box526
FEATURE [Part::MultiFuse] Fusion526
  Shapes = -> [Cut630,Cylinder796]
FEATURE [Part::Cut] Cut631
  Base = -> Fusion526
  Tool = -> Cylinder778
FEATURE [Part::Chamfer] Chamfer099  label="central-axle-steering-knukle"
  Base = -> Cut631
  Edges = 3 edges r=1: [Edge81,Edge82,Edge84]
FEATURE [Part::Box] Box527  label="Cube727"
  Height = 10
  Length = 10
  Placement = pos=(299.5,53,-35) rot=(0,0,1;0rad)
  Width = 6
FEATURE [Part::Cut] Cut632
  Base = -> Fillet350
  Tool = -> Box527
FEATURE [Part::Cut] Cut633
  Base = -> Cut632
  Tool = -> Fusion521
FEATURE [Part::Chamfer] Chamfer100  label="central-axle-susp-left-attach"
  Base = -> Cut633
  Edges = 1 edges r=1: [Edge9]
FEATURE [Part::Cylinder] Cylinder
  Angle = 360
  Height = 18
  Radius = 7.5
FEATURE [Part::Cylinder] Cylinder806  label="Cylinder990"
  Angle = 360
  Height = 18
  Radius = 5
FEATURE [Part::Cut] Cut
  Base = -> Cylinder
  Tool = -> Cylinder806
FEATURE [Part::Cylinder] Cylinder807  label="Cylinder991"
  Angle = 360
  Height = 4
  Radius = 5.6
FEATURE [Part::Cylinder] Cylinder808  label="Cylinder992"
  Angle = 360
  Height = 15
  Placement = pos=(0,0,6) rot=(0,0,1;0rad)
  Radius = 5.6
FEATURE [Part::MultiFuse] Fusion
  Shapes = -> [Cylinder808,Cylinder807]
FEATURE [Part::Cut] Cut001
  Base = -> Cut
  Tool = -> Fusion
FEATURE [Part::Cylinder] Cylinder004
  Angle = 360
  Height = 15
  Placement = pos=(0,0,10) rot=(0,0,1;0rad)
  Radius = 6
FEATURE [Part::Cut] Cut634
  Base = -> Cut001
  Tool = -> Cylinder004
FEATURE [Part::Cylinder] Cylinder809  label="Cylinder993"
  Angle = 360
  Height = 22.7
  Placement = pos=(-11,0,15.5) rot=(0,1,0;1.5708rad)
  Radius = 4
FEATURE [Part::Cylinder] Cylinder810  label="Cylinder994"
  Angle = 360
  Height = 15
  Placement = pos=(0,0,10) rot=(0,0,1;0rad)
  Radius = 6
FEATURE [Part::Cut] Cut635
  Base = -> Cylinder809
  Tool = -> Cylinder810
FEATURE [Part::Cylinder] Cylinder811  label="Cylinder995"
  Angle = 360
  Height = 22.7
  Placement = pos=(-11,0,15.5) rot=(0,1,0;1.5708rad)
  Radius = 1.25
FEATURE [Part::MultiFuse] Fusion527
  Shapes = -> [Cut634,Cut635]
FEATURE [Part::Cut] Cut636
  Base = -> Fusion527
  Placement = pos=(0,0,0) rot=(0,-1,0;1.5708rad)
  Tool = -> Cylinder811
FEATURE [Part::Box] Box
  Height = 24
  Length = 5
  Placement = pos=(-2.5,0,0) rot=(0,0,1;0rad)
  Width = 32
FEATURE [Part::Cylinder] Cylinder812  label="Cylinder996"
  Angle = 360
  Height = 30
  Radius = 6
FEATURE [Part::Cut] Cut637
  Base = -> Box
  Tool = -> Cylinder812
FEATURE [Part::Box] Box001
  Height = 10
  Length = 10
  Placement = pos=(-4,2,18) rot=(0,0,1;0rad)
  Width = 10
FEATURE [Part::Cut] Cut638
  Base = -> Cut637
  Tool = -> Box001
FEATURE [Part::Box] Box002
  Height = 10
  Length = 10
  Placement = pos=(-4,-2.5,-6) rot=(0,0,1;0rad)
  Width = 38
FEATURE [Part::Cut] Cut007
  Base = -> Cut638
  Tool = -> Box002
FEATURE [Part::Box] Box003
  Height = 14
  Length = 10
  Placement = pos=(-4,21,2.5) rot=(0,0,1;0rad)
  Width = 11
FEATURE [Part::Box] Box528
  Height = 10
  Length = 10
  Placement = pos=(-6,12,18) rot=(1,0,0;0.593412rad)
  Width = 12
FEATURE [Part::Cut] Cut008
  Base = -> Cut007
  Tool = -> Box528
FEATURE [Part::Cut] Cut009
  Base = -> Cut008
  Tool = -> Box003
FEATURE [Part::Box] Box529
  Height = 20
  Length = 10
  Placement = pos=(-4,8,4) rot=(1,0,0;0.750491rad)
  Width = 32
FEATURE [Part::Box] Box530
  Height = 16.5
  Length = 10
  Placement = pos=(-4,8,0) rot=(0,0,1;0rad)
  Width = 17
FEATURE [Part::Cut] Cut010
  Base = -> Box530
  Tool = -> Box529
FEATURE [Part::Cut] Cut011
  Base = -> Cut009
  Tool = -> Cut010
FEATURE [Part::Cylinder] Cylinder009
  Angle = 360
  Height = 10
  Placement = pos=(-4,28.25,20.25) rot=(0,1,0;1.5708rad)
  Radius = 1.25
FEATURE [Part::Cut] Cut639
  Base = -> Cut011
  Placement = pos=(0,0,0) rot=(0,-1,0;1.5708rad)
  Tool = -> Cylinder009
FEATURE [Part::Cylinder] Cylinder010
  Angle = 360
  Height = 10
  Placement = pos=(-4,28.25,20.25) rot=(0,1,0;1.5708rad)
  Radius = 1.25
FEATURE [Part::Cut] Cut641
  Base = -> Cut009
  Tool = -> Cut010
FEATURE [Part::Cut] Cut640
  Base = -> Cut641
  Placement = pos=(0,0,0) rot=(-0.707107,0,0.707107;3.14159rad)
  Tool = -> Cylinder010
FEATURE [Part::Cone] Cone002
  Angle = 360
  Height = 3.4
  Placement = pos=(0,0,-0.4) rot=(0,0,1;0rad)
  Radius1 = 3.1
  Radius2 = 3.6
FEATURE [Part::Cylinder] Cylinder029
  Angle = 360
  Height = 15
  Placement = pos=(0,0,3) rot=(0,0,1;0rad)
  Radius = 4.1
FEATURE [Part::Box] Box531
  Height = 15
  Length = 9.2
  Placement = pos=(-4.6,-4,3) rot=(0,0,1;0rad)
  Width = 8.1
FEATURE [Part::MultiFuse] Fusion016
  Shapes = -> [Cone002,Box531,Cylinder029]
FEATURE [Part::Cylinder] Cylinder030
  Angle = 360
  Height = 14
  Placement = pos=(0,10,10.5) rot=(1,0,0;1.5708rad)
  Radius = 7
FEATURE [Part::Cylinder] Cylinder031
  Angle = 360
  Height = 10
  Placement = pos=(0,4.1,10.5) rot=(1,0,0;1.5708rad)
  Radius = 7.5
FEATURE [Part::Cylinder] Cylinder032
  Angle = 360
  Height = 20
  Placement = pos=(-10,-5,10.5) rot=(0,1,0;1.5708rad)
  Radius = 6
FEATURE [Part::MultiFuse] Fusion529
  Shapes = -> [Fusion016,Cylinder030,Cylinder031]
FEATURE [Part::Cut] Cut038
  Base = -> Fusion529
  Tool = -> Cylinder032
FEATURE [Part::Cylinder] Cylinder033
  Angle = 360
  Height = 20
  Placement = pos=(0,14,10.5) rot=(1,0,0;1.5708rad)
  Radius = 6
FEATURE [Part::Cut] Cut039
  Base = -> Cut038
  Tool = -> Cylinder033
FEATURE [Part::Cylinder] Cylinder034
  Angle = 360
  Height = 21
  Placement = pos=(0,4.7,0) rot=(0,0,1;0rad)
  Radius = 8.4
FEATURE [Part::Cylinder] Cylinder035
  Angle = 120
  Height = 21
  Placement = pos=(0,2.4,0) rot=(0,0,1;3.66519rad)
  Radius = 12.5
FEATURE [Part::Cut] Cut040
  Base = -> Cylinder035
  Tool = -> Cylinder034
FEATURE [Part::Cut] Cut041
  Base = -> Cut039
  Tool = -> Cut040
FEATURE [Part::Fillet] Fillet009
  Base = -> Cut041
  Edges = 4 edges r=3.5: [Edge16,Edge18,Edge21,Edge29]
  Placement = pos=(0,0,0.4) rot=(0,0,1;0rad)
FEATURE [Part::Box] Box030
  Height = 4.8
  Length = 1.61
  Placement = pos=(6,1,8.5) rot=(0,0,1;0rad)
  Width = 9
FEATURE [Part::Feature] Face004
  shape: bbox 14.42 x 11.68 x 2e-07 mm, 1 faces, 0 solids (baked)
FEATURE [Part::Extrusion] Extrude004
  Base = -> Face004
  Dir = (0,0,4.8)
  Placement = pos=(0,0,0.1) rot=(0,0,1;0rad)
  Solid = false
FEATURE [Part::Feature] Face005
  shape: bbox 23.76 x 23.56 x 2e-07 mm, 1 faces, 0 solids (baked)
FEATURE [Part::Extrusion] Extrude005
  Base = -> Face005
  Dir = (0,0,4.8)
  Placement = pos=(0.01,0,-4.8) rot=(0,0,1;0rad)
  Solid = false
FEATURE [Part::Cylinder] Cylinder036
  Angle = 360
  Height = 15
  Placement = pos=(28,-5,0) rot=(0,0,1;0rad)
  Radius = 1.25
FEATURE [Part::Cylinder] Cylinder037
  Angle = 360
  Height = 15
  Placement = pos=(24,-5,0) rot=(0,0,1;0rad)
  Radius = 1.25
FEATURE [Part::MultiFuse] Fusion019
  Shapes = -> [Cylinder037,Cylinder036]
FEATURE [Part::Cut] Cut042
  Base = -> Extrude004
  Placement = pos=(0,0,-4.8) rot=(0,0,1;0rad)
  Tool = -> Fusion019
FEATURE [Part::Feature] Face006
  Placement = pos=(-1,0,0) rot=(0,0,1;0rad)
  shape: bbox 34.38 x 24.68 x 2.001e-07 mm, 1 faces, 0 solids (baked)
FEATURE [Part::Extrusion] Extrude006
  Base = -> Face006
  Dir = (0,0,4.8)
  Solid = false
FEATURE [Part::MultiFuse] Fusion530
  Shapes = -> [Extrude006,Box030]
FEATURE [Part::Cylinder] Cylinder038
  Angle = 360
  Height = 15
  Placement = pos=(28,-5,0) rot=(0,0,1;0rad)
  Radius = 1.25
FEATURE [Part::Cylinder] Cylinder039
  Angle = 360
  Height = 15
  Placement = pos=(24,-5,0) rot=(0,0,1;0rad)
  Radius = 1.25
FEATURE [Part::Feature] Face008
  Placement = pos=(-19.94,7.36,12) rot=(0,0,-1;0.802851rad)
  shape: bbox 46.85 x 21.29 x 2.017e-07 mm, 1 faces, 0 solids (baked)
FEATURE [Part::Extrusion] Extrude007
  Base = -> Face008
  Dir = (0,0,5)
  Solid = false
FEATURE [Part::Cylinder] Cylinder040
  Angle = 360
  Height = 15
  Placement = pos=(0,13,10.9) rot=(1,0,0;1.5708rad)
  Radius = 7.1
FEATURE [Part::Cylinder] Cylinder041
  Angle = 360
  Height = 18
  Placement = pos=(0,11.3,10.9) rot=(1,0,0;1.5708rad)
  Radius = 6
FEATURE [Part::MultiFuse] Fusion531
  Shapes = -> [Cylinder041,Cylinder040]
FEATURE [Part::Cut] Cut047
  Base = -> Extrude007
  Tool = -> Fusion531
FEATURE [Part::MultiFuse] Fusion532
  Shapes = -> [Fusion530,Fillet009]
FEATURE [Part::MultiFuse] Fusion533
  Shapes = -> [Cylinder039,Cylinder038]
FEATURE [Part::Cut] Cut048
  Base = -> Fusion532
  Tool = -> Fusion533
FEATURE [Part::Cut] Cut049
  Base = -> Cut047
  Tool = -> Cut048
FEATURE [Part::Cylinder] Cylinder042
  Angle = 360
  Height = 10
  Placement = pos=(-28,-5,0.3) rot=(0,0,1;0rad)
  Radius = 1.25
FEATURE [Part::Cut] Cut050
  Base = -> Cut049
  Tool = -> Cylinder042
FEATURE [Part::Cylinder] Cylinder043
  Angle = 360
  Height = 15
  Placement = pos=(0,13,10.9) rot=(1,0,0;1.5708rad)
  Radius = 7.1
FEATURE [Part::Cylinder] Cylinder044
  Angle = 360
  Height = 18
  Placement = pos=(0,11.3,10.9) rot=(1,0,0;1.5708rad)
  Radius = 6
FEATURE [Part::MultiFuse] Fusion534
  Shapes = -> [Cylinder044,Cylinder043]
FEATURE [Part::MultiFuse] Fusion535
  Shapes = -> [Extrude005,Cut042]
FEATURE [Part::Box] Box532
  Height = 10
  Length = 4
  Placement = pos=(7.5,-3,0) rot=(0,0,1;0rad)
  Width = 15
FEATURE [Part::Cut] Cut051
  Base = -> Cut050
  Tool = -> Box532
FEATURE [Part::Box] Box533
  Height = 10
  Length = 7
  Placement = pos=(7.5,7.5,0.3) rot=(0,0,1;0rad)
  Width = 8
FEATURE [Part::Cut] Cut052
  Base = -> Fusion535
  Tool = -> Box533
FEATURE [Part::Box] Box534
  Height = 8.2
  Length = 7
  Placement = pos=(3.5,-3,0.3) rot=(0,0,1;0rad)
  Width = 10.5
FEATURE [Part::Cylinder] Cylinder046
  Angle = 360
  Height = 32
  Placement = pos=(-10,-5,10.9) rot=(0,1,0;1.5708rad)
  Radius = 6
FEATURE [Part::MultiFuse] Fusion029
  Shapes = -> [Fusion534,Cylinder046]
FEATURE [Part::MultiFuse] Fusion031
  Shapes = -> [Cylinder039,Cylinder038]
FEATURE [Part::MultiFuse] Fusion030
  Shapes = -> [Fusion530,Fillet009]
FEATURE [Part::Cut] Cut054
  Base = -> Fusion030
  Tool = -> Fusion031
FEATURE [Part::Box] Box036
  Height = 4.8
  Length = 8
  Placement = pos=(5.5,-3,3.7) rot=(0,0,1;0rad)
  Width = 3.5
FEATURE [Part::MultiFuse] Fusion032
  Shapes = -> [Box036,Box534]
FEATURE [Part::Cut] Cut055
  Base = -> Fusion032
  Tool = -> Fusion029
FEATURE [Part::Cut] Cut056
  Base = -> Cut055
  Tool = -> Cut054
FEATURE [Part::MultiFuse] Fusion033
  Shapes = -> [Cut052,Cut051,Cut056]
FEATURE [Part::Chamfer] Chamfer002
  Base = -> Fusion033
  Edges = 1 edges r=2.99: [Edge67]
FEATURE [Part::Cylinder] Cylinder047
  Angle = 360
  Height = 10
  Placement = pos=(10,-5,0) rot=(0,0,1;0rad)
  Radius = 4
FEATURE [Part::Cut] Cut057
  Base = -> Chamfer002
  Tool = -> Cylinder047
FEATURE [Part::Fillet] Fillet010
  Base = -> Cut057
  Edges = 1 edges r=1.2: [Edge52]
FEATURE [Part::Cylinder] Cylinder048
  Angle = 80
  Height = 3
  Placement = pos=(0,3,3.4) rot=(0,0,1;4.01426rad)
  Radius = 7
FEATURE [Part::Cut] Cut058
  Base = -> Fillet010
  Tool = -> Cylinder048
FEATURE [Part::Cylinder] Cylinder049
  Angle = 80
  Height = 3
  Placement = pos=(0,0,3.4) rot=(0,0,1;4.01426rad)
  Radius = 4.2
FEATURE [Part::Cut] Cut059
  Base = -> Cut058
  Tool = -> Cylinder049
FEATURE [Part::Box] Box535
  Height = 6
  Length = 11
  Placement = pos=(-5.5,-2,3.4) rot=(0,0,1;0rad)
  Width = 6.5
FEATURE [Part::Cut] Cut060
  Base = -> Cut059
  Tool = -> Box535
FEATURE [Part::Cylinder] Cylinder050
  Angle = 360
  Height = 15
  Placement = pos=(0,13,10.9) rot=(1,0,0;1.5708rad)
  Radius = 7.5
FEATURE [Part::Cut] Cut061
  Base = -> Cut060
  Tool = -> Cylinder050
FEATURE [Part::Box] Box038
  Height = 10
  Length = 14.5
  Placement = pos=(-23,0.5,-10.5) rot=(0.678599,0.281084,0.678599;1.09606rad)
  Width = 10
FEATURE [Part::Cut] Cut062
  Base = -> Cut061
  Tool = -> Box038
FEATURE [Part::Box] Box039
  Height = 10
  Length = 10
  Placement = pos=(-1.5,-2,13) rot=(0,1,0;0.925025rad)
  Width = 10
FEATURE [Part::Cut] Cut063
  Base = -> Cut062
  Tool = -> Box039
FEATURE [Part::Box] Box041  label="Cube001"
  Height = 4.5
  Length = 8
  Placement = pos=(-4,-25,-9.2) rot=(0,0,1;0rad)
  Width = 25
FEATURE [Part::Cylinder] Cylinder052
  Angle = 360
  Height = 4.5
  Placement = pos=(0,0,-9.2) rot=(0,0,1;0rad)
  Radius = 3.5
FEATURE [Part::Cylinder] Cylinder053
  Angle = 360
  Height = 4.5
  Placement = pos=(0,0,-9.2) rot=(0,0,1;0rad)
  Radius = 5
FEATURE [Part::MultiFuse] Fusion034
  Shapes = -> [Cylinder053,Box041]
FEATURE [Part::Fillet] Fillet011
  Base = -> Fusion034
  Edges = 2 edges r=3.99: [Edge2,Edge4]
FEATURE [Part::Box] Box042  label="Cube002"
  Height = 4.5
  Length = 43
  Placement = pos=(-22,-8.5,-9.2) rot=(0,0,1;0rad)
  Width = 7.5
FEATURE [Part::Box] Box043  label="Cube003"
  Height = 5
  Length = 7
  Placement = pos=(-22,-8.5,-4.7) rot=(0,0,1;0rad)
  Width = 7.5
FEATURE [Part::Box] Box044  label="Cube004"
  Height = 5
  Length = 7
  Placement = pos=(14,-8.5,-4.7) rot=(0,0,1;0rad)
  Width = 7.5
FEATURE [Part::Cylinder] Cylinder055
  Angle = 360
  Height = 5.7
  Placement = pos=(17.5,-4.75,0.3) rot=(0,0,1;0rad)
  Radius = 3.5
FEATURE [Part::Cylinder] Cylinder056
  Angle = 360
  Height = 2
  Placement = pos=(-18.5,-4.75,0.3) rot=(0,0,1;0rad)
  Radius = 3.5
FEATURE [Part::Cylinder] Cylinder057
  Angle = 360
  Height = 20
  Placement = pos=(17.5,-4.75,-9.7) rot=(0,0,1;0rad)
  Radius = 0.85
FEATURE [Part::Cylinder] Cylinder058
  Angle = 360
  Height = 5
  Placement = pos=(-18.5,-4.75,-1.7) rot=(0,0,1;0rad)
  Radius = 0.9
FEATURE [Part::MultiFuse] Fusion036
  Shapes = -> [Box042,Box043,Box044,Fillet011]
FEATURE [Part::Cylinder] Cylinder059
  Angle = 360
  Height = 4.5
  Placement = pos=(0,-21,-9.2) rot=(0,0,1;0rad)
  Radius = 1.25
FEATURE [Part::Cut] Cut066
  Base = -> Fusion036
  Tool = -> Cylinder052
FEATURE [Part::Chamfer] Chamfer003
  Base = -> Cut066
  Edges = 2 edges r=6: [Edge29,Edge33]
FEATURE [Part::Fillet] Fillet012
  Base = -> Chamfer003
  Edges = 4 edges r=3.5: [Edge4,Edge26,Edge42,Edge51]
FEATURE [Part::Cut] Cut067
  Base = -> Fillet012
  Tool = -> Cylinder059
FEATURE [Part::Cylinder] Cylinder060
  Angle = 360
  Height = 20
  Placement = pos=(17.5,-4.75,-9.7) rot=(0,0,1;0rad)
  Radius = 1.2
FEATURE [Part::Cylinder] Cylinder061
  Angle = 360
  Height = 20
  Placement = pos=(-18.5,-4.75,-9.7) rot=(0,0,1;0rad)
  Radius = 1.2
FEATURE [Part::Cylinder] Cylinder062
  Angle = 360
  Height = 8
  Placement = pos=(-18.5,-4.75,-1.7) rot=(0,0,1;0rad)
  Radius = 0.85
FEATURE [Part::Cut] Cut070
  Base = -> Cylinder056
  Tool = -> Cylinder058
FEATURE [Part::Cut] Cut071
  Base = -> Cut063
  Tool = -> Cylinder062
FEATURE [Part::MultiFuse] Fusion037
  Shapes = -> [Cut070,Cut071]
FEATURE [Part::MultiFuse] Fusion038
  Shapes = -> [Fusion037,Cylinder055]
FEATURE [Part::Cut] Cut072
  Base = -> Fusion038
  Tool = -> Cylinder057
FEATURE [Part::Cylinder] Cylinder063
  Angle = 360
  Height = 5
  Placement = pos=(17.5,-4.75,-9.2) rot=(0,0,1;0rad)
  Radius = 2
FEATURE [Part::Cylinder] Cylinder064
  Angle = 360
  Height = 5
  Placement = pos=(-18.5,-4.75,-9.2) rot=(0,0,1;0rad)
  Radius = 2
FEATURE [Part::MultiFuse] Fusion039
  Shapes = -> [Cylinder060,Cylinder063]
FEATURE [Part::MultiFuse] Fusion040
  Shapes = -> [Cylinder064,Cylinder061]
FEATURE [Part::MultiFuse] Fusion041
  Shapes = -> [Fusion039,Fusion040]
FEATURE [Part::Cut] Cut073  label="Cut68"
  Base = -> Cut067
  Placement = pos=(98,16.5,-39) rot=(1,0,0;3.14159rad)
  Tool = -> Fusion041
FEATURE [Part::Box] Box045  label="Cube005"
  Height = 10
  Length = 10
  Placement = pos=(-33,-9,0) rot=(0,0,1;0rad)
  Width = 10
FEATURE [Part::Box] Box046  label="Cube006"
  Height = 10
  Length = 10
  Placement = pos=(-33,0.3,0) rot=(0,0,-1;0.733038rad)
  Width = 10
FEATURE [Part::MultiFuse] Fusion042
  Shapes = -> [Box046,Box045]
FEATURE [Part::Cut] Cut074
  Base = -> Cut072
  Tool = -> Fusion042
FEATURE [Part::Fillet] Fillet013  label="front-axle-steering-knukle-arm-lower"
  Base = -> Cut074
  Edges = 2 edges r=1: [Edge166,Edge167]
  Placement = pos=(98,16.5,-39) rot=(1,0,0;3.14159rad)
FEATURE [Part::Cylinder] Cylinder813  label="Cylinder997"
  Angle = 360
  Height = 10
  Placement = pos=(0,0,0.5) rot=(0,0,1;0rad)
  Radius = 23.5
FEATURE [Part::Cylinder] Cylinder814  label="Cylinder998"
  Angle = 360
  Height = 17
  Radius = 22
FEATURE [Part::Cut] Cut647
  Base = -> Cylinder813
  Placement = pos=(0,0,4.5) rot=(0,0,1;0rad)
  Tool = -> Cylinder814
FEATURE [Part::Cylinder] Cylinder815
  Angle = 360
  Height = 20
  Radius = 23.5
FEATURE [Part::Cylinder] Cylinder816
  Angle = 360
  Height = 17
  Radius = 23.5
FEATURE [Part::Cylinder] Cylinder817
  Angle = 360
  Height = 17
  Radius = 22.1
FEATURE [Part::Cut] Cut649
  Base = -> Cylinder816
  Placement = pos=(0,0,1.5) rot=(0,0,1;0rad)
  Tool = -> Cylinder817
FEATURE [Part::Cut] Cut648
  Base = -> Cylinder815
  Tool = -> Cut649
FEATURE [Part::MultiFuse] Fusion537
  Shapes = -> [Cut647,Cut648]
FEATURE [Part::Cylinder] Cylinder818
  Angle = 360
  Height = 20
  Radius = 18.5
FEATURE [Part::Cut] Cut646
  Base = -> Fusion537
  Tool = -> Cylinder818
FEATURE [Part::Cylinder] Cylinder819
  Angle = 360
  Height = 10
  Placement = pos=(0,0,15) rot=(0,0,1;0rad)
  Radius = 20.5
FEATURE [Part::Cut] Cut645
  Base = -> Cut646
  Tool = -> Cylinder819
FEATURE [Part::Fillet] Fillet002
  Base = -> Cut645
  Edges = 1 edges r=1: [Edge20]
FEATURE [Part::Cone] Cone
  Angle = 360
  Height = 7
  Placement = pos=(0,0,15) rot=(0,0,1;0rad)
  Radius1 = 21
  Radius2 = 15
FEATURE [Part::Cylinder] Cylinder820
  Angle = 360
  Height = 26
  Radius = 10
FEATURE [Part::Cut] Cut651
  Base = -> Cone
  Tool = -> Cylinder820
FEATURE [Part::Cone] Cone001
  Angle = 360
  Height = 10
  Placement = pos=(0,0,9) rot=(0,0,1;0rad)
  Radius1 = 24
  Radius2 = 15
FEATURE [Part::Cut] Cut650
  Base = -> Cut651
  Tool = -> Cone001
FEATURE [Part::MultiFuse] Fusion536
  Shapes = -> [Fillet002,Cut650]
FEATURE [Part::Cylinder] Cylinder821
  Angle = 360
  Height = 12
  Radius = 20
FEATURE [Part::Cut] Cut644
  Base = -> Fusion536
  Tool = -> Cylinder821
FEATURE [Part::Chamfer] Chamfer001
  Base = -> Cut644
  Edges = 1 edges r=1.49: [Edge39]
FEATURE [Part::Chamfer] Chamfer101
  Base = -> Chamfer001
  Edges = 1 edges r=2: [Edge10]
FEATURE [Part::Cylinder] Cylinder822
  Angle = 360
  Height = 8
  Placement = pos=(12,0,16) rot=(0,1,0;1.01229rad)
  Radius = 2.5
FEATURE [Part::Cylinder] Cylinder823
  Angle = 360
  Height = 8
  Placement = pos=(12,0,16) rot=(0,1,0;1.01229rad)
  Radius = 2.5
FEATURE [Part::Mirroring] Part__Mirroring  label="Cylinder107 (Mirror #1)004"
  Base = (0,0,0)
  Normal = (1,0,0)
  Source = -> Cylinder823
FEATURE [Part::MultiFuse] Fusion539
  Shapes = -> [Cylinder822,Part__Mirroring]
FEATURE [Part::Cylinder] Cylinder011
  Angle = 360
  Height = 8
  Placement = pos=(12,0,16) rot=(0,1,0;1.01229rad)
  Radius = 2.5
FEATURE [Part::Cylinder] Cylinder012
  Angle = 360
  Height = 8
  Placement = pos=(12,0,16) rot=(0,1,0;1.01229rad)
  Radius = 2.5
FEATURE [Part::Mirroring] Part__Mirroring001  label="Cylinder107 (Mirror #1)005"
  Base = (0,0,0)
  Normal = (1,0,0)
  Source = -> Cylinder012
FEATURE [Part::MultiFuse] Fusion540
  Placement = pos=(0,0,0) rot=(0,0,1;0.628319rad)
  Shapes = -> [Cylinder011,Part__Mirroring001]
FEATURE [Part::Cylinder] Cylinder013
  Angle = 360
  Height = 8
  Placement = pos=(12,0,16) rot=(0,1,0;1.01229rad)
  Radius = 2.5
FEATURE [Part::Cylinder] Cylinder014
  Angle = 360
  Height = 8
  Placement = pos=(12,0,16) rot=(0,1,0;1.01229rad)
  Radius = 2.5
FEATURE [Part::Mirroring] Part__Mirroring002  label="Cylinder107 (Mirror #1)006"
  Base = (0,0,0)
  Normal = (1,0,0)
  Source = -> Cylinder014
FEATURE [Part::MultiFuse] Fusion005
  Placement = pos=(0,0,0) rot=(0,0,1;1.25664rad)
  Shapes = -> [Cylinder013,Part__Mirroring002]
FEATURE [Part::Cylinder] Cylinder015
  Angle = 360
  Height = 8
  Placement = pos=(12,0,16) rot=(0,1,0;1.01229rad)
  Radius = 2.5
FEATURE [Part::Cylinder] Cylinder824
  Angle = 360
  Height = 8
  Placement = pos=(12,0,16) rot=(0,1,0;1.01229rad)
  Radius = 2.5
FEATURE [Part::Mirroring] Part__Mirroring003  label="Cylinder107 (Mirror #1)007"
  Base = (0,0,0)
  Normal = (1,0,0)
  Source = -> Cylinder824
FEATURE [Part::MultiFuse] Fusion006
  Placement = pos=(0,0,0) rot=(0,0,1;1.88496rad)
  Shapes = -> [Cylinder015,Part__Mirroring003]
FEATURE [Part::Cylinder] Cylinder825
  Angle = 360
  Height = 8
  Placement = pos=(12,0,16) rot=(0,1,0;1.01229rad)
  Radius = 2.5
FEATURE [Part::Cylinder] Cylinder826
  Angle = 360
  Height = 8
  Placement = pos=(12,0,16) rot=(0,1,0;1.01229rad)
  Radius = 2.5
FEATURE [Part::Mirroring] Part__Mirroring004  label="Cylinder107 (Mirror #1)008"
  Base = (0,0,0)
  Normal = (1,0,0)
  Source = -> Cylinder826
FEATURE [Part::MultiFuse] Fusion007
  Placement = pos=(0,0,0) rot=(0,0,1;2.51327rad)
  Shapes = -> [Cylinder825,Part__Mirroring004]
FEATURE [Part::MultiFuse] Fusion538
  Placement = pos=(0,0,-1) rot=(0,0,1;0rad)
  Shapes = -> [Fusion539,Fusion540,Fusion005,Fusion006,Fusion007]
FEATURE [Part::Cut] Cut643
  Base = -> Chamfer101
  Tool = -> Fusion538
FEATURE [Part::Cylinder] Cylinder827
  Angle = 360
  Height = 10
  Placement = pos=(12.5,0,13) rot=(0,0,1;0rad)
  Radius = 1.1
FEATURE [Part::Cylinder] Cylinder828
  Angle = 360
  Height = 10
  Placement = pos=(-12.5,0,13) rot=(0,0,1;0rad)
  Radius = 1.1
FEATURE [Part::MultiFuse] Fusion009
  Placement = pos=(0,0,0) rot=(0,0,1;0.314159rad)
  Shapes = -> [Cylinder827,Cylinder828]
FEATURE [Part::Cylinder] Cylinder829
  Angle = 360
  Height = 10
  Placement = pos=(12.5,0,13) rot=(0,0,1;0rad)
  Radius = 1.1
FEATURE [Part::Cylinder] Cylinder830
  Angle = 360
  Height = 10
  Placement = pos=(-12.5,0,13) rot=(0,0,1;0rad)
  Radius = 1.1
FEATURE [Part::MultiFuse] Fusion010
  Placement = pos=(0,0,0) rot=(0,0,1;0.942478rad)
  Shapes = -> [Cylinder829,Cylinder830]
FEATURE [Part::Cylinder] Cylinder023
  Angle = 360
  Height = 10
  Placement = pos=(12.5,0,13) rot=(0,0,1;0rad)
  Radius = 1.1
FEATURE [Part::Cylinder] Cylinder831
  Angle = 360
  Height = 10
  Placement = pos=(-12.5,0,13) rot=(0,0,1;0rad)
  Radius = 1.1
FEATURE [Part::MultiFuse] Fusion011
  Placement = pos=(0,0,0) rot=(0,0,1;2.82743rad)
  Shapes = -> [Cylinder023,Cylinder831]
FEATURE [Part::Cylinder] Cylinder832
  Angle = 360
  Height = 10
  Placement = pos=(12.5,0,13) rot=(0,0,1;0rad)
  Radius = 1.1
FEATURE [Part::Cylinder] Cylinder833  label="Cylinder999"
  Angle = 360
  Height = 10
  Placement = pos=(-12.5,0,13) rot=(0,0,1;0rad)
  Radius = 1.1
FEATURE [Part::MultiFuse] Fusion012
  Placement = pos=(0,0,0) rot=(0,0,1;2.19911rad)
  Shapes = -> [Cylinder832,Cylinder833]
FEATURE [Part::Cylinder] Cylinder834  label="Cylinder1000"
  Angle = 360
  Height = 10
  Placement = pos=(12.5,0,13) rot=(0,0,1;0rad)
  Radius = 1.1
FEATURE [Part::Cylinder] Cylinder835  label="Cylinder1001"
  Angle = 360
  Height = 10
  Placement = pos=(-12.5,0,13) rot=(0,0,1;0rad)
  Radius = 1.1
FEATURE [Part::MultiFuse] Fusion013
  Placement = pos=(0,0,0) rot=(0,0,1;1.5708rad)
  Shapes = -> [Cylinder834,Cylinder835]
FEATURE [Part::MultiFuse] Fusion541
  Shapes = -> [Fusion009,Fusion010,Fusion011,Fusion012,Fusion013]
FEATURE [Part::Cut] Cut642
  Base = -> Cut643
  Tool = -> Fusion541
FEATURE [Part::Fillet] Fillet001
  Base = -> Cut642
  Edges = 1 edges r=1.5: [Edge121]
FEATURE [Part::Fillet] Fillet  label="rim"
  Base = -> Fillet001
  Edges = 1 edges r=1.5: [Edge161]
FEATURE [Part::Cylinder] Cylinder836  label="Cylinder1002"
  Angle = 360
  Height = 4
  Placement = pos=(0,0,12) rot=(0,0,1;0rad)
  Radius = 15
FEATURE [Part::Cylinder] Cylinder837  label="Cylinder1003"
  Angle = 360
  Height = 3
  Placement = pos=(0,0,16) rot=(0,0,1;0rad)
  Radius = 15
FEATURE [Part::Cylinder] Cylinder838  label="Cylinder1004"
  Angle = 360
  Height = 7
  Placement = pos=(0,0,19) rot=(0,0,1;0rad)
  Radius = 10
FEATURE [Part::Cylinder] Cylinder839  label="Cylinder1005"
  Angle = 360
  Height = 4
  Placement = pos=(0,0,23) rot=(0,0,1;0rad)
  Radius = 8
FEATURE [Part::Cut] Cut655
  Base = -> Cylinder838
  Tool = -> Cylinder839
FEATURE [Part::MultiFuse] Fusion544
  Shapes = -> [Cylinder837,Cut655]
FEATURE [Part::MultiFuse] Fusion543
  Shapes = -> [Cylinder836,Fusion544]
FEATURE [Part::Cylinder] Cylinder840  label="Cylinder1006"
  Angle = 360
  Height = 3
  Placement = pos=(0,0,12) rot=(0,0,1;0.139626rad)
  Radius = 18.4
FEATURE [Part::Cylinder] Cylinder841  label="Cylinder1007"
  Angle = 360
  Height = 3
  Placement = pos=(0,0,12) rot=(0,0,1;1.39626rad)
  Radius = 18.4
FEATURE [Part::Cylinder] Cylinder842  label="Cylinder1008"
  Angle = 360
  Height = 3
  Placement = pos=(0,0,12) rot=(0,0,1;2.6529rad)
  Radius = 18.4
FEATURE [Part::Cylinder] Cylinder843  label="Cylinder1009"
  Angle = 360
  Height = 3
  Placement = pos=(0,0,12) rot=(0,0,1;3.90954rad)
  Radius = 18.4
FEATURE [Part::Cylinder] Cylinder844  label="Cylinder1010"
  Angle = 360
  Height = 3
  Placement = pos=(0,0,12) rot=(0,0,-1;1.11701rad)
  Radius = 18.4
FEATURE [Part::MultiFuse] Fusion545
  Shapes = -> [Cylinder840,Cylinder841,Cylinder842,Cylinder843,Cylinder844]
FEATURE [Part::MultiFuse] Fusion542
  Shapes = -> [Fusion543,Fusion545]
FEATURE [Part::Cylinder] Cylinder845  label="Cylinder1011"
  Angle = 360
  Height = 17
  Placement = pos=(0,0,9) rot=(0,0,1;0rad)
  Radius = 2
FEATURE [Part::Cut] Cut654
  Base = -> Fusion542
  Tool = -> Cylinder845
FEATURE [Part::Feature] Face
  shape: bbox 17.79 x 17.28 x 2e-07 mm, 1 faces, 0 solids (baked)
FEATURE [Part::Extrusion] Extrude
  Base = -> Face
  Dir = (0,0,6)
  Placement = pos=(0,0,16) rot=(0,0,1;0rad)
  Solid = false
FEATURE [Part::Cylinder] Cylinder846  label="Cylinder1012"
  Angle = 360
  Height = 4
  Placement = pos=(0,0,12) rot=(0,0,1;0rad)
  Radius = 10
FEATURE [Part::MultiFuse] Fusion018
  Placement = pos=(0,0,-1) rot=(0,0,1;0rad)
  Shapes = -> [Extrude,Cylinder846]
FEATURE [Part::Cut] Cut653
  Base = -> Cut654
  Tool = -> Fusion018
FEATURE [Part::Cylinder] Cylinder847  label="Cylinder1013"
  Angle = 360
  Height = 10
  Placement = pos=(12.5,0,13) rot=(0,0,1;0rad)
  Radius = 0.8
FEATURE [Part::Cylinder] Cylinder848  label="Cylinder1014"
  Angle = 360
  Height = 10
  Placement = pos=(-12.5,0,13) rot=(0,0,1;0rad)
  Radius = 0.8
FEATURE [Part::MultiFuse] Fusion547
  Placement = pos=(0,0,0) rot=(0,0,1;0.314159rad)
  Shapes = -> [Cylinder847,Cylinder848]
FEATURE [Part::Cylinder] Cylinder849
  Angle = 360
  Height = 10
  Placement = pos=(12.5,0,13) rot=(0,0,1;0rad)
  Radius = 0.8
FEATURE [Part::Cylinder] Cylinder850
  Angle = 360
  Height = 10
  Placement = pos=(-12.5,0,13) rot=(0,0,1;0rad)
  Radius = 0.8
FEATURE [Part::MultiFuse] Fusion021
  Placement = pos=(0,0,0) rot=(0,0,1;0.942478rad)
  Shapes = -> [Cylinder849,Cylinder850]
FEATURE [Part::Cylinder] Cylinder851
  Angle = 360
  Height = 10
  Placement = pos=(12.5,0,13) rot=(0,0,1;0rad)
  Radius = 0.8
FEATURE [Part::Cylinder] Cylinder045
  Angle = 360
  Height = 10
  Placement = pos=(-12.5,0,13) rot=(0,0,1;0rad)
  Radius = 0.8
FEATURE [Part::MultiFuse] Fusion548
  Placement = pos=(0,0,0) rot=(0,0,1;2.82743rad)
  Shapes = -> [Cylinder851,Cylinder045]
FEATURE [Part::Cylinder] Cylinder852  label="Cylinder1015"
  Angle = 360
  Height = 10
  Placement = pos=(12.5,0,13) rot=(0,0,1;0rad)
  Radius = 0.8
FEATURE [Part::Cylinder] Cylinder853  label="Cylinder1016"
  Angle = 360
  Height = 10
  Placement = pos=(-12.5,0,13) rot=(0,0,1;0rad)
  Radius = 0.8
FEATURE [Part::MultiFuse] Fusion549
  Placement = pos=(0,0,0) rot=(0,0,1;2.19911rad)
  Shapes = -> [Cylinder852,Cylinder853]
FEATURE [Part::Cylinder] Cylinder854  label="Cylinder1017"
  Angle = 360
  Height = 10
  Placement = pos=(12.5,0,13) rot=(0,0,1;0rad)
  Radius = 0.8
FEATURE [Part::Cylinder] Cylinder855  label="Cylinder1018"
  Angle = 360
  Height = 10
  Placement = pos=(-12.5,0,13) rot=(0,0,1;0rad)
  Radius = 0.8
FEATURE [Part::MultiFuse] Fusion550
  Placement = pos=(0,0,0) rot=(0,0,1;1.5708rad)
  Shapes = -> [Cylinder854,Cylinder855]
FEATURE [Part::MultiFuse] Fusion546
  Placement = pos=(0,0,-2) rot=(0,0,1;0rad)
  Shapes = -> [Fusion547,Fusion021,Fusion548,Fusion549,Fusion550]
FEATURE [Part::Cut] Cut652  label="hub-front"
  Base = -> Cut653
  Placement = pos=(98,16,-51) rot=(1,0,0;1.5708rad)
  Tool = -> Fusion546
FEATURE [Part::Cylinder] Cylinder073
  Angle = 360
  Height = 26
  Radius = 10.1
FEATURE [Part::Cut] Cut656  label="rim-front"
  Base = -> Fillet
  Placement = pos=(98,16,-51) rot=(1,0,0;1.5708rad)
  Tool = -> Cylinder073
FEATURE [Part::Cylinder] Cylinder856  label="Cylinder1019"
  Angle = 360
  Height = 4
  Radius = 5.6
FEATURE [Part::Cylinder] Cylinder857  label="Cylinder1020"
  Angle = 360
  Height = 22.7
  Placement = pos=(-11,0,15.5) rot=(0,1,0;1.5708rad)
  Radius = 1.25
FEATURE [Part::Cylinder] Cylinder858  label="Cylinder1021"
  Angle = 360
  Height = 18
  Radius = 7.5
FEATURE [Part::Cylinder] Cylinder859  label="Cylinder1022"
  Angle = 360
  Height = 18
  Radius = 5
FEATURE [Part::Cut] Cut660
  Base = -> Cylinder858
  Tool = -> Cylinder859
FEATURE [Part::Cylinder] Cylinder860  label="Cylinder1023"
  Angle = 360
  Height = 15
  Placement = pos=(0,0,6) rot=(0,0,1;0rad)
  Radius = 5.6
FEATURE [Part::MultiFuse] Fusion552
  Shapes = -> [Cylinder860,Cylinder856]
FEATURE [Part::Cut] Cut658
  Base = -> Cut660
  Tool = -> Fusion552
FEATURE [Part::Cylinder] Cylinder861  label="Cylinder1024"
  Angle = 360
  Height = 22.7
  Placement = pos=(-11,0,15.5) rot=(0,1,0;1.5708rad)
  Radius = 4
FEATURE [Part::Cylinder] Cylinder862
  Angle = 360
  Height = 15
  Placement = pos=(0,0,10) rot=(0,0,1;0rad)
  Radius = 6
FEATURE [Part::Cut] Cut661
  Base = -> Cut658
  Tool = -> Cylinder862
FEATURE [Part::Cylinder] Cylinder863  label="Cylinder1025"
  Angle = 360
  Height = 15
  Placement = pos=(0,0,10) rot=(0,0,1;0rad)
  Radius = 6
FEATURE [Part::Cut] Cut659
  Base = -> Cylinder861
  Tool = -> Cylinder863
FEATURE [Part::MultiFuse] Fusion551
  Shapes = -> [Cut661,Cut659]
FEATURE [Part::Cut] Cut657
  Base = -> Fusion551
  Placement = pos=(0,0,0) rot=(0,-1,0;1.5708rad)
  Tool = -> Cylinder857
FEATURE [Part::MultiFuse] Fusion553  label="front-axle-steering-knukle-left"
  Placement = pos=(98,1,-51) rot=(0,0,-1;1.5708rad)
  Shapes = -> [Cut639,Cut636]
FEATURE [Part::MultiFuse] Fusion554  label="front-axle-steering-knukle-right"
  Placement = pos=(98,168,-51) rot=(0,0,1;1.5708rad)
  Shapes = -> [Cut657,Cut640]
FEATURE [Part::Box] Box536  label="Cube"
  Height = 20
  Length = 40.6
  Placement = pos=(-0.3,0,0) rot=(0,0,1;0rad)
  Width = 38
FEATURE [Part::Cylinder] Cylinder864  label="Cylinder1026"
  Angle = 360
  Height = 10
  Placement = pos=(10,5,10) rot=(1,0,0;1.5708rad)
  Radius = 2.8
FEATURE [Part::Box] Box537  label="Cube728"
  Height = 20
  Length = 53.4
  Placement = pos=(-6.7,7,0) rot=(0,0,1;0rad)
  Width = 4
FEATURE [Part::Box] Box538  label="Cube729"
  Height = 12
  Length = 12
  Placement = pos=(389.5,39.75,-32) rot=(0,0,1;0rad)
  Width = 13.75
FEATURE [Part::Box] Box539  label="Cube730"
  Height = 8
  Length = 12
  Placement = pos=(389.5,41.75,-32) rot=(0,0,1;0rad)
  Width = 7.5
FEATURE [Part::Cut] Cut663  label="Cut892"
  Base = -> Box538
  Tool = -> Box539
FEATURE [Part::Box] Box540  label="Cube731"
  Height = 10
  Length = 30
  Placement = pos=(373.5,49.75,-20) rot=(0,0,1;0rad)
  Width = 3.75
FEATURE [Part::MultiFuse] Fusion556
  Placement = pos=(-350,0,2) rot=(0,0,1;0rad)
  Shapes = -> [Box540,Cut663]
FEATURE [Part::Box] Box541  label="Cube732"
  Height = 14
  Length = 22
  Placement = pos=(23.5,49.75,-18) rot=(0,0,1;0rad)
  Width = 3.75
FEATURE [Part::Cylinder] Cylinder866  label="Cylinder1027"
  Angle = 360
  Height = 20
  Placement = pos=(49.5,56.5,-13) rot=(1,0,0;1.5708rad)
  Radius = 1.6
FEATURE [Part::MultiFuse] Fusion557
  Shapes = -> [Box541,Fusion556]
FEATURE [Part::Box] Box542  label="Cube733"
  Height = 14
  Length = 16
  Placement = pos=(29.5,39.75,-18) rot=(0,0,1;0rad)
  Width = 13
FEATURE [Part::MultiFuse] Fusion558
  Shapes = -> [Fusion557,Box542]
FEATURE [Part::Cylinder] Cylinder867  label="Cylinder1028"
  Angle = 360
  Height = 10
  Placement = pos=(28.5,49.75,-11) rot=(1,0,0;1.5708rad)
  Radius = 2.8
FEATURE [Part::Cut] Cut664
  Base = -> Fusion558
  Tool = -> Cylinder867
FEATURE [Part::Cylinder] Cylinder868  label="Cylinder1029"
  Angle = 360
  Height = 6.75
  Placement = pos=(28.5,56.5,-11) rot=(1,0,0;1.5708rad)
  Radius = 1.6
FEATURE [Part::Cylinder] Cylinder869  label="Cylinder1030"
  Angle = 360
  Height = 20
  Placement = pos=(45.5,56.5,-26) rot=(1,0,0;1.5708rad)
  Radius = 2.1
FEATURE [Part::MultiFuse] Fusion559
  Shapes = -> [Cylinder868,Cylinder866,Cylinder869]
FEATURE [Part::Cut] Cut665
  Base = -> Cut664
  Tool = -> Fusion559
FEATURE [Part::Cylinder] Cylinder870  label="Cylinder1031"
  Angle = 360
  Height = 14
  Placement = pos=(38,53.5,-11) rot=(1,0,0;1.5708rad)
  Radius = 3.5
FEATURE [Part::Cylinder] Cylinder871  label="Cylinder1032"
  Angle = 360
  Height = 4
  Placement = pos=(38,43.75,-11) rot=(1,0,0;1.5708rad)
  Radius = 5.6
FEATURE [Part::Cylinder] Cylinder872  label="Cylinder1033"
  Angle = 360
  Height = 4.5
  Placement = pos=(38,53.5,-11) rot=(1,0,0;1.5708rad)
  Radius = 5.6
FEATURE [Part::MultiFuse] Fusion560
  Placement = pos=(-1,0,0) rot=(0,0,1;0rad)
  Shapes = -> [Cylinder870,Cylinder872,Cylinder871]
FEATURE [Part::Cut] Cut666
  Base = -> Cut665
  Tool = -> Fusion560
FEATURE [Part::Fillet] Fillet352
  Base = -> Cut666
  Edges = 4 edges r=4: [Edge38,Edge40,Edge44,Edge47]
FEATURE [Part::Fillet] Fillet353
  Base = -> Fillet352
  Edges = 2 edges r=3: [Edge36,Edge65]
FEATURE [Part::Cylinder] Cylinder873  label="Cylinder1034"
  Angle = 360
  Height = 5
  Placement = pos=(49.5,49.75,-13) rot=(1,0,0;1.5708rad)
  Radius = 3.1
FEATURE [Part::Fillet] Fillet354
  Base = -> Fillet353
  Edges = 1 edges r=3: [Edge31]
FEATURE [Part::Cut] Cut667
  Base = -> Fillet354
  Tool = -> Cylinder873
FEATURE [Part::Fillet] Fillet355
  Base = -> Cut667
  Edges = 2 edges r=4: [Edge83,Edge86]
FEATURE [Part::Fillet] Fillet356
  Base = -> Fillet355
  Edges = 3 edges r=3: [Edge23,Edge40,Edge43]
FEATURE [Part::Box] Box543  label="Cube734"
  Height = 2
  Length = 16
  Placement = pos=(37.5,49.75,-20) rot=(0,0,1;0rad)
  Width = 3.75
FEATURE [Part::Chamfer] Chamfer102
  Base = -> Box543
  Edges = 2 edges r=1.99: [Edge4,Edge8]
FEATURE [Part::Cylinder] Cylinder874  label="Cylinder1035"
  Angle = 360
  Height = 20
  Placement = pos=(28.5,56.5,-11) rot=(1,0,0;1.5708rad)
  Radius = 1.6
FEATURE [Part::Cylinder] Cylinder875  label="Cylinder1036"
  Angle = 360
  Height = 20
  Placement = pos=(49.5,56.5,-13) rot=(1,0,0;1.5708rad)
  Radius = 1.6
FEATURE [Part::Box] Box544  label="Cube735"
  Height = 14
  Length = 30
  Placement = pos=(23.5,49.75,-18) rot=(0,0,1;0rad)
  Width = 3.75
FEATURE [Part::Cylinder] Cylinder876  label="Cylinder1037"
  Angle = 360
  Height = 20
  Placement = pos=(37,56.5,-11) rot=(1,0,0;1.5708rad)
  Radius = 1.6
FEATURE [Part::MultiFuse] Fusion562
  Shapes = -> [Cylinder874,Cylinder875,Cylinder876]
FEATURE [Part::Box] Box545  label="Cube736"
  Height = 8
  Length = 1.9
  Placement = pos=(29.5,39.75,-15) rot=(0,0,1;0rad)
  Width = 10
FEATURE [Part::Cut] Cut668  label="leafspring-mount-front-left-HOLES"
  Base = -> Box544
  Tool = -> Fusion562
FEATURE [Part::Cylinder] Cylinder877  label="Cylinder1038"
  Angle = 360
  Height = 11
  Placement = pos=(29.8503,50.5822,-11) rot=(0.990855,-0.095409,-0.095409;1.57998rad)
  Radius = 2.8
FEATURE [Part::Cut] Cut669
  Base = -> Box545
  Tool = -> Cylinder877
FEATURE [Part::MultiFuse] Fusion563  label="leafspring-mount-front-left-int-servo"
  Shapes = -> [Cut669,Fillet356,Chamfer102]
FEATURE [Part::Box] Box548  label="Cube739"
  Height = 4.5
  Length = 15
  Placement = pos=(90,10,-34.25) rot=(1,0,0;0.785398rad)
  Width = 13
FEATURE [Part::Cut] Cut670  label="front-axle-steering-knukle-arm-upper"
  Base = -> Cut073
  Tool = -> Box548
FEATURE [Part::Cylinder] Cylinder878  label="Cylinder1039"
  Angle = 360
  Height = 6
  Placement = pos=(37,39.75,-11) rot=(1,0,0;1.5708rad)
  Radius = 7
FEATURE [Part::Box] Box549  label="Cube740"
  Height = 22
  Length = 6
  Placement = pos=(34,33.75,-33) rot=(0,0,1;0rad)
  Width = 4
FEATURE [Part::Cylinder] Cylinder880  label="Cylinder1040"
  Angle = 360
  Height = 4
  Placement = pos=(37,37.75,-33) rot=(1,0,0;1.5708rad)
  Radius = 4
FEATURE [Part::Cylinder] Cylinder881  label="Cylinder1041"
  Angle = 360
  Height = 4
  Placement = pos=(37,37.75,-24) rot=(1,0,0;1.5708rad)
  Radius = 4
FEATURE [Part::MultiFuse] Fusion564
  Placement = pos=(0,-5,0) rot=(0,0,1;0rad)
  Shapes = -> [Cylinder881,Box549,Cylinder880,Cylinder878]
FEATURE [Part::Cylinder] Cylinder882  label="Cylinder1042"
  Angle = 360
  Height = 4
  Placement = pos=(37,32.75,-24) rot=(1,0,0;1.5708rad)
  Radius = 1.25
FEATURE [Part::Cylinder] Cylinder883  label="Cylinder1043"
  Angle = 360
  Height = 4
  Placement = pos=(37,32.75,-33) rot=(1,0,0;1.5708rad)
  Radius = 1.25
FEATURE [Part::Cylinder] Cylinder884  label="Cylinder1044"
  Angle = 360
  Height = 4
  Placement = pos=(37,39.75,-11) rot=(1,0,0;1.5708rad)
  Radius = 5.6
FEATURE [Part::Cylinder] Cylinder885  label="Cylinder1045"
  Angle = 360
  Height = 11
  Placement = pos=(37,39.75,-11) rot=(1,0,0;1.5708rad)
  Radius = 2.6
FEATURE [Part::Cylinder] Cylinder886  label="Cylinder1046"
  Angle = 360
  Height = 6
  Placement = pos=(37,39.75,-11) rot=(1,0,0;1.5708rad)
  Radius = 8
FEATURE [Part::MultiFuse] Fusion565
  Shapes = -> [Cylinder886,Fusion564]
FEATURE [Part::MultiFuse] Fusion566
  Shapes = -> [Cylinder882,Cylinder885,Cylinder883,Cylinder884]
FEATURE [Part::Cut] Cut671
  Base = -> Fusion565
  Tool = -> Fusion566
FEATURE [Part::Chamfer] Chamfer103
  Base = -> Cut671
  Edges = 1 edges r=0.99: [Edge4]
FEATURE [Part::Cylinder] Cylinder887  label="Cylinder1047"
  Angle = 360
  Height = 7
  Placement = pos=(37,37.75,-8) rot=(0,0,1;0rad)
  Radius = 1.25
FEATURE [Part::Cut] Cut672
  Base = -> Chamfer103
  Tool = -> Cylinder887
FEATURE [Part::Chamfer] Chamfer104  label="front-axle-steering-arm-int-servo"
  Base = -> Cut672
  Edges = 20 edges r=0.5: [Edge10,Edge12,Edge19,Edge20,Edge21,Edge22,Edge23,Edge24,Edge25,Edge26,Edge27,Edge31,Edge33,Edge34,Edge35,Edge36,Edge37,Edge38,Edge39,Edge40]
FEATURE [Part::Cylinder] Cylinder889  label="front-steering-rod"
  Angle = 360
  Height = 63
  Placement = pos=(37,35.5,-33) rot=(-0.074596,0.994785,0.069562;1.5062rad)
  Radius = 1.5
FEATURE [Part::Box] Box550  label="Cube741"
  Height = 21
  Length = 41
  Placement = pos=(19.5,64.5,-21.5) rot=(0,0,1;0rad)
  Width = 41
FEATURE [Part::Cylinder] Cylinder891  label="Cylinder1048"
  Angle = 360
  Height = 11
  Placement = pos=(37,64.5,-11) rot=(1,0,0;1.5708rad)
  Radius = 6
FEATURE [Part::Cylinder] Cylinder893  label="Cylinder1049"
  Angle = 360
  Height = 10
  Placement = pos=(13.5,83,-11) rot=(0,1,0;1.5708rad)
  Radius = 1.6
FEATURE [Part::Cylinder] Cylinder894  label="Cylinder1050"
  Angle = 360
  Height = 10
  Placement = pos=(13.5,91,-11) rot=(0,1,0;1.5708rad)
  Radius = 1.6
FEATURE [Part::Cylinder] Cylinder895  label="Cylinder1051"
  Angle = 360
  Height = 2.5
  Placement = pos=(13.5,91,-11) rot=(0,1,0;1.5708rad)
  Radius = 3.1
FEATURE [Part::Cylinder] Cylinder896  label="Cylinder1052"
  Angle = 360
  Height = 2.5
  Placement = pos=(13.5,83,-11) rot=(0,1,0;1.5708rad)
  Radius = 3.1
FEATURE [Part::Cylinder] Cylinder726  label="Cylinder833"
  Angle = 360
  Height = 15
  Placement = pos=(395.5,54,-28) rot=(1,0,0;1.5708rad)
  Radius = 2.1
FEATURE [Part::Box] Box482  label="Cube684"
  Height = 12
  Length = 12
  Placement = pos=(389.5,39.75,-32) rot=(0,0,1;0rad)
  Width = 13.75
FEATURE [Part::Box] Box483  label="Cube685"
  Height = 8
  Length = 12
  Placement = pos=(389.5,41.75,-32) rot=(0,0,1;0rad)
  Width = 7.5
FEATURE [Part::Cut] Cut594  label="Cut873"
  Base = -> Box482
  Tool = -> Box483
FEATURE [Part::Box] Box484  label="Cube686"
  Height = 10
  Length = 16
  Placement = pos=(387.5,49.75,-20) rot=(0,0,1;0rad)
  Width = 3.75
FEATURE [Part::Cylinder] Cylinder727  label="Cylinder834"
  Angle = 360
  Height = 15
  Placement = pos=(391.5,54,-15) rot=(1,0,0;1.5708rad)
  Radius = 1.6
FEATURE [Part::Cylinder] Cylinder728  label="Cylinder835"
  Angle = 360
  Height = 15
  Placement = pos=(399.5,54,-15) rot=(1,0,0;1.5708rad)
  Radius = 1.6
FEATURE [Part::MultiFuse] Fusion475
  Shapes = -> [Box484,Cut594]
FEATURE [Part::Fillet] Fillet334
  Base = -> Fusion475
  Edges = 3 edges r=3: [Edge6,Edge7,Edge16]
FEATURE [Part::Fillet] Fillet335
  Base = -> Fillet334
  Edges = 4 edges r=4: [Edge29,Edge32,Edge40,Edge43]
FEATURE [Part::Chamfer] Chamfer081
  Base = -> Fillet335
  Edges = 2 edges r=1.99: [Edge21,Edge44]
FEATURE [Part::Cylinder] Cylinder729  label="Cylinder836"
  Angle = 360
  Height = 2
  Placement = pos=(391.5,49.75,-15) rot=(1,0,0;1.5708rad)
  Radius = 3.1
FEATURE [Part::Cylinder] Cylinder730  label="Cylinder837"
  Angle = 360
  Height = 2
  Placement = pos=(399.5,49.75,-15) rot=(1,0,0;1.5708rad)
  Radius = 3.1
FEATURE [Part::MultiFuse] Fusion476
  Shapes = -> [Cylinder729,Cylinder730,Cylinder726,Cylinder728,Cylinder727]
FEATURE [Part::Cut] Cut593  label="leafspring-mount-front-left"
  Base = -> Chamfer081
  Placement = pos=(-350,0,2) rot=(0,0,1;0rad)
  Tool = -> Fusion476
FEATURE [App::DocumentObjectGroup] Group001  label="TLT-mounts"
  Group = -> [Fillet013,Fusion553,Fusion554,Cut670]
FEATURE [Part::MultiFuse] Fusion585  label="union"
  Placement = pos=(27,66.5,-21) rot=(0,0,1;0rad)
  Shapes = -> [Box537,Box536,Cylinder864]
FEATURE [Part::Cylinder] Cylinder930  label="servo-shaft"
  Angle = 360
  Height = 31.25
  Placement = pos=(37,60,-11) rot=(1,0,0;1.5708rad)
  Radius = 2.5
FEATURE [Part::Cylinder] Cylinder931  label="Cylinder1074"
  Angle = 360
  Height = 10
  Placement = pos=(0,6.35,-6.7) rot=(0,0,1;0rad)
  Radius = 5.35
FEATURE [Part::Feature] servo_shaft_coupler001001_solid  label="servo_shaft_coupler002 (Solid)"
  shape: bbox 10.67 x 10.67 x 12.7 mm, 306 faces (baked)
FEATURE [Part::Cylinder] Cylinder932  label="Cylinder1075"
  Angle = 360
  Height = 10
  Placement = pos=(0,6.35,-13.7) rot=(0,0,1;0rad)
  Radius = 5.5
FEATURE [Part::MultiFuse] Fusion586
  Shapes = -> [servo_shaft_coupler001001_solid,Cylinder931]
FEATURE [Part::Cut] Cut684
  Base = -> Fusion586
  Tool = -> Cylinder932
FEATURE [Part::Cylinder] Cylinder933  label="Cylinder1076"
  Angle = 360
  Height = 10
  Placement = pos=(0,6.35,-5.7) rot=(0,0,1;0rad)
  Radius = 1.5
FEATURE [Part::Cut] Cut685
  Base = -> Cut684
  Tool = -> Cylinder933
FEATURE [Part::Cylinder] Cylinder934  label="Cylinder1077"
  Angle = 360
  Height = 10
  Placement = pos=(0,6.35,-7.7) rot=(0,0,1;0rad)
  Radius = 2.6
FEATURE [Part::Cut] Cut686
  Base = -> Cut685
  Tool = -> Cylinder934
FEATURE [Part::Cylinder] Cylinder935  label="Cylinder1078"
  Angle = 360
  Height = 4
  Placement = pos=(0,6.35,-2.7) rot=(0,0,1;0rad)
  Radius = 4
FEATURE [Part::Cut] Cut687
  Base = -> Cut686
  Placement = pos=(0,0,0) rot=(0,1,0;3.14159rad)
  Tool = -> Cylinder935
FEATURE [Part::Cylinder] Cylinder936  label="Cylinder1079"
  Angle = 360
  Height = 10
  Placement = pos=(0,7,0.7) rot=(1,0,0;1.5708rad)
  Radius = 1.25
FEATURE [Part::Cut] Cut688  label="servo-shaft-coupler"
  Base = -> Cut687
  Placement = pos=(37,58.75,-17.35) rot=(1,0,0;1.5708rad)
  Tool = -> Cylinder936
FEATURE [Part::Cylinder] Cylinder937  label="Cylinder1080"
  Angle = 360
  Height = 10
  Radius = 5.2
FEATURE [Part::Box] Box555  label="Cube746"
  Height = 10
  Length = 16
  Placement = pos=(-8,-10,0) rot=(0,0,1;0rad)
  Width = 20
FEATURE [Part::Cut] Cut689
  Base = -> Box555
  Tool = -> Cylinder937
FEATURE [Part::Cylinder] Cylinder938  label="Cylinder1081"
  Angle = 360
  Height = 10
  Placement = pos=(0,10,2) rot=(1,0,0;1.5708rad)
  Radius = 1.25
FEATURE [Part::Cylinder] Cylinder939  label="Cylinder1082"
  Angle = 360
  Height = 20
  Placement = pos=(0,10,7.5) rot=(1,0,0;1.5708rad)
  Radius = 1.25
FEATURE [Part::MultiFuse] Fusion587
  Shapes = -> [Cylinder939,Cylinder938]
FEATURE [Part::Cut] Cut690  label="servo-shaft-coupler-HOLES"
  Base = -> Cut689
  Placement = pos=(37,73,-11) rot=(1,0,0;1.5708rad)
  Tool = -> Fusion587
FEATURE [Part::Cylinder] Cylinder940  label="Cylinder1083"
  Angle = 360
  Height = 1
  Placement = pos=(37,66.5,-11) rot=(1,0,0;1.5708rad)
  Radius = 6.5
FEATURE [Part::MultiFuse] Fusion588  label="steering-servo"
  Placement = pos=(1,0,0) rot=(0,0,1;0rad)
  Shapes = -> [Fusion585,Cylinder940]
FEATURE [Part::Box] Box556  label="Cube747"
  Height = 20
  Length = 8
  Placement = pos=(19.5,79.5,-21) rot=(0,0,1;0rad)
  Width = 15
FEATURE [Part::Box] Box557  label="Cube748"
  Height = 17
  Length = 7
  Placement = pos=(67.5,79.5,-19.5) rot=(0,0,1;0rad)
  Width = 15
FEATURE [Part::Cylinder] Cylinder945  label="Cylinder1090"
  Angle = 360
  Height = 5
  Placement = pos=(37,64.5,-11) rot=(1,0,0;1.5708rad)
  Radius = 7
FEATURE [Part::Cylinder] Cylinder946  label="Cylinder1093"
  Angle = 360
  Height = 10
  Placement = pos=(13.5,91,-11) rot=(0,1,0;1.5708rad)
  Radius = 1.25
FEATURE [Part::Cylinder] Cylinder947  label="Cylinder1094"
  Angle = 360
  Height = 10
  Placement = pos=(13.5,83,-11) rot=(0,1,0;1.5708rad)
  Radius = 1.25
FEATURE [Part::MultiFuse] Fusion593
  Shapes = -> [Cylinder895,Cylinder893,Cylinder894,Cylinder896]
FEATURE [Part::MultiFuse] Fusion594
  Placement = pos=(4,0,0) rot=(0,0,1;0rad)
  Shapes = -> [Cylinder946,Cylinder947]
FEATURE [Part::Cut] Cut693
  Base = -> Box556
  Tool = -> Fusion594
FEATURE [Part::Cylinder] Cylinder948  label="Cylinder1099"
  Angle = 360
  Height = 15
  Placement = pos=(27,85,-10.2) rot=(1,0,0;1.5708rad)
  Radius = 0.9
FEATURE [Part::Cylinder] Cylinder949  label="Cylinder1100"
  Angle = 360
  Height = 15
  Placement = pos=(27,85,0) rot=(1,0,0;1.5708rad)
  Radius = 0.9
FEATURE [Part::MultiFuse] Fusion595
  Placement = pos=(-4.2,9.5,-5.9) rot=(0,0,1;0rad)
  Shapes = -> [Cylinder949,Cylinder948]
FEATURE [Part::Cylinder] Cylinder950  label="Cylinder1101"
  Angle = 360
  Height = 15
  Placement = pos=(27,85,-10.2) rot=(1,0,0;1.5708rad)
  Radius = 0.9
FEATURE [Part::Cylinder] Cylinder951  label="Cylinder1102"
  Angle = 360
  Height = 15
  Placement = pos=(27,85,0) rot=(1,0,0;1.5708rad)
  Radius = 0.9
FEATURE [Part::MultiFuse] Fusion596
  Placement = pos=(44.2,9.5,-5.9) rot=(0,0,1;0rad)
  Shapes = -> [Cylinder951,Cylinder950]
FEATURE [Part::Cut] Cut694  label="steering-servo-front-mount"
  Base = -> Cut693
  Tool = -> Fusion595
FEATURE [Part::Box] Box558  label="Cube749"
  Height = 17
  Length = 5
  Placement = pos=(74.5,55,-19.5) rot=(0,0,1;0rad)
  Width = 60
FEATURE [Part::MultiFuse] Fusion597
  Shapes = -> [Box557,Box558]
FEATURE [Part::Cut] Cut695
  Base = -> Fusion597
  Tool = -> Fusion596
FEATURE [Part::Fillet] Fillet357  label="steering-servo-rear-mount"
  Base = -> Cut695
  Edges = 4 edges r=3: [Edge11,Edge13,Edge21,Edge23]
  Placement = pos=(1,0,0) rot=(0,0,1;0rad)
FEATURE [Part::Box] Box559  label="Cube750"
  Height = 17
  Length = 10
  Placement = pos=(37,55,-19.5) rot=(0,0,1;0rad)
  Width = 10
FEATURE [Part::MultiFuse] Fusion598
  Shapes = -> [Box559,Box550,Cylinder891,Cylinder945]
FEATURE [Part::Cut] Cut696
  Base = -> Cut581
  Tool = -> Fusion598
FEATURE [Part::Cut] Cut697  label="cross-member-front"
  Base = -> Cut696
  Tool = -> Fusion593
FEATURE [Part::Cylinder] Cylinder952  label="Cylinder1115"
  Angle = 360
  Height = 10
  Placement = pos=(3,60,10) rot=(1,0,0;1.5708rad)
  Radius = 1.2
FEATURE [Part::Cylinder] Cylinder953  label="Cylinder1116"
  Angle = 360
  Height = 10
  Placement = pos=(3,10,10) rot=(1,0,0;1.5708rad)
  Radius = 1.2
FEATURE [Part::Box] Box560  label="Cube751"
  Height = 17
  Length = 16
  Placement = pos=(-2,0,1.5) rot=(0,0,1;0rad)
  Width = 60
FEATURE [Part::Box] Box561  label="Cube752"
  Height = 25.5
  Length = 10
  Placement = pos=(-12,0,-5) rot=(0,0,1;0rad)
  Width = 63
FEATURE [Part::Cylinder] Cylinder954  label="Cylinder1117"
  Angle = 360
  Height = 11
  Placement = pos=(-2,66.5,4) rot=(0,1,0;1.5708rad)
  Radius = 1.25
FEATURE [Part::Cylinder] Cylinder955  label="Cylinder1118"
  Angle = 360
  Height = 11
  Placement = pos=(-2,13.5,4) rot=(0,1,0;1.5708rad)
  Radius = 1.25
FEATURE [Part::Cylinder] Cylinder956  label="Cylinder1119"
  Angle = 360
  Height = 15
  Placement = pos=(-2,57,20) rot=(0,1,0;1.5708rad)
  Radius = 1.25
FEATURE [Part::Cylinder] Cylinder957  label="Cylinder1120"
  Angle = 360
  Height = 15
  Placement = pos=(-2,23,20) rot=(0,1,0;1.5708rad)
  Radius = 1.25
FEATURE [Part::MultiFuse] Fusion599
  Placement = pos=(-10,-10,1) rot=(0,0,1;0rad)
  Shapes = -> [Cylinder954,Cylinder957,Cylinder955,Cylinder956]
FEATURE [Part::Fillet] Fillet358
  Base = -> Box561
  Edges = 4 edges r=3: [Edge9,Edge10,Edge11,Edge12]
  Placement = pos=(25.5,53.5,-16.5) rot=(0,0,1;0rad)
FEATURE [Part::Fillet] Fillet359
  Base = -> Box560
  Edges = 4 edges r=3: [Edge9,Edge10,Edge11,Edge12]
  Placement = pos=(25.5,55,-21) rot=(0,0,1;0rad)
FEATURE [Part::MultiFuse] Fusion600
  Placement = pos=(0,0,2) rot=(0,0,1;0rad)
  Shapes = -> [Cylinder952,Cylinder953]
FEATURE [Part::MultiFuse] Fusion601
  Placement = pos=(25.5,55,-23) rot=(0,0,1;0rad)
  Shapes = -> [Fusion599,Fusion600]
FEATURE [Part::Box] Box562  label="Cube753"
  Height = 26
  Length = 41
  Placement = pos=(19.5,64.5,-21.5) rot=(0,0,1;0rad)
  Width = 41
FEATURE [Part::Cylinder] Cylinder958  label="Cylinder1121"
  Angle = 360
  Height = 11
  Placement = pos=(37,64.5,-11) rot=(1,0,0;1.5708rad)
  Radius = 6
FEATURE [Part::Cylinder] Cylinder959  label="Cylinder1122"
  Angle = 360
  Height = 10
  Placement = pos=(13.5,83,-11) rot=(0,1,0;1.5708rad)
  Radius = 1.6
FEATURE [Part::Cylinder] Cylinder960  label="Cylinder1123"
  Angle = 360
  Height = 10
  Placement = pos=(13.5,91,-11) rot=(0,1,0;1.5708rad)
  Radius = 1.6
FEATURE [Part::Cylinder] Cylinder961  label="Cylinder1124"
  Angle = 360
  Height = 2.5
  Placement = pos=(13.5,91,-11) rot=(0,1,0;1.5708rad)
  Radius = 3.1
FEATURE [Part::Cylinder] Cylinder962  label="Cylinder1125"
  Angle = 360
  Height = 2.5
  Placement = pos=(13.5,83,-11) rot=(0,1,0;1.5708rad)
  Radius = 3.1
FEATURE [Part::Cylinder] Cylinder963  label="Cylinder1126"
  Angle = 360
  Height = 5
  Placement = pos=(37,64.5,-11) rot=(1,0,0;1.5708rad)
  Radius = 7
FEATURE [Part::MultiFuse] Fusion603
  Shapes = -> [Cylinder961,Cylinder959,Cylinder960,Cylinder962]
FEATURE [Part::Box] Box563  label="Cube754"
  Height = 17
  Length = 10
  Placement = pos=(37,55,-19.5) rot=(0,0,1;0rad)
  Width = 10
FEATURE [Part::MultiFuse] Fusion604
  Shapes = -> [Box563,Box562,Cylinder958,Cylinder963]
FEATURE [Part::MultiFuse] Fusion605
  Shapes = -> [Fillet359,Fillet358]
FEATURE [Part::Cut] Cut698
  Base = -> Fusion605
  Tool = -> Fusion601
FEATURE [Part::Cut] Cut699
  Base = -> Cut698
  Tool = -> Fusion604
FEATURE [Part::Cut] Cut700  label="cross-member-front-lifted"
  Base = -> Cut699
  Tool = -> Fusion603
FEATURE [App::DocumentObjectGroup] Group  label="to-be -removed"
  Group = -> [Cut697,Cut593]
FEATURE [App::DocumentObjectGroup] Group002  label="tools"
  Group = -> [Cut690,Cut668]
FEATURE [App::DocumentObjectGroup] Group003  label="suspensions"
  Group = -> [Fusion091,Fusion439,Fusion440,Fusion008,Fusion459,Cut021]
FEATURE [Part::Cylinder] Cylinder964  label="Cylinder1136"
  Angle = 360
  Height = 6
  Placement = pos=(37,39.75,-11) rot=(1,0,0;1.5708rad)
  Radius = 7
FEATURE [Part::Box] Box564  label="Cube755"
  Height = 22
  Length = 6
  Placement = pos=(34,33.75,-33) rot=(0,0,1;0rad)
  Width = 4
FEATURE [Part::Cylinder] Cylinder965  label="Cylinder1137"
  Angle = 360
  Height = 4
  Placement = pos=(37,37.75,-33) rot=(1,0,0;1.5708rad)
  Radius = 4
FEATURE [Part::Cylinder] Cylinder968  label="Cylinder1140"
  Angle = 360
  Height = 4
  Placement = pos=(37,32.75,-33) rot=(1,0,0;1.5708rad)
  Radius = 1.25
FEATURE [Part::Cylinder] Cylinder969  label="Cylinder1141"
  Angle = 360
  Height = 4
  Placement = pos=(37,39.75,-11) rot=(1,0,0;1.5708rad)
  Radius = 5.6
FEATURE [Part::Cylinder] Cylinder970  label="Cylinder1142"
  Angle = 360
  Height = 11
  Placement = pos=(37,39.75,-11) rot=(1,0,0;1.5708rad)
  Radius = 2.6
FEATURE [Part::Cylinder] Cylinder971  label="Cylinder1143"
  Angle = 360
  Height = 6
  Placement = pos=(37,39.75,-11) rot=(1,0,0;1.5708rad)
  Radius = 8
FEATURE [Part::Cylinder] Cylinder972  label="Cylinder1144"
  Angle = 360
  Height = 7
  Placement = pos=(37,37.75,-8) rot=(0,0,1;0rad)
  Radius = 1.25
FEATURE [Part::MultiFuse] Fusion607
  Shapes = -> [Cylinder969,Cylinder968,Cylinder972,Cylinder970]
FEATURE [Part::MultiFuse] Fusion608
  Placement = pos=(0,-5,0) rot=(0,0,1;0rad)
  Shapes = -> [Box564,Cylinder964,Cylinder965]
FEATURE [Part::MultiFuse] Fusion609
  Shapes = -> [Fusion608,Cylinder971]
FEATURE [Part::Cylinder] Cylinder973  label="Cylinder1152"
  Angle = 360
  Height = 6
  Placement = pos=(37,39.75,-11) rot=(1,0,0;1.5708rad)
  Radius = 7
FEATURE [Part::Box] Box565  label="Cube756"
  Height = 22
  Length = 6
  Placement = pos=(34,33.75,-33) rot=(0,0,1;0rad)
  Width = 4
FEATURE [Part::Cylinder] Cylinder974  label="Cylinder1153"
  Angle = 360
  Height = 4
  Placement = pos=(37,37.75,-33) rot=(1,0,0;1.5708rad)
  Radius = 4
FEATURE [Part::Cylinder] Cylinder975  label="Cylinder1154"
  Angle = 360
  Height = 4
  Placement = pos=(37,32.75,-33) rot=(1,0,0;1.5708rad)
  Radius = 1.25
FEATURE [Part::Cylinder] Cylinder976  label="Cylinder1155"
  Angle = 360
  Height = 4
  Placement = pos=(37,39.75,-11) rot=(1,0,0;1.5708rad)
  Radius = 5.6
FEATURE [Part::Cylinder] Cylinder977  label="Cylinder1156"
  Angle = 360
  Height = 11
  Placement = pos=(37,39.75,-11) rot=(1,0,0;1.5708rad)
  Radius = 2.6
FEATURE [Part::Cylinder] Cylinder978  label="Cylinder1157"
  Angle = 360
  Height = 6
  Placement = pos=(37,39.75,-11) rot=(1,0,0;1.5708rad)
  Radius = 8
FEATURE [Part::Cylinder] Cylinder979  label="Cylinder1158"
  Angle = 360
  Height = 7
  Placement = pos=(37,37.75,-8) rot=(0,0,1;0rad)
  Radius = 1.25
FEATURE [Part::Cylinder] Cylinder980  label="Cylinder1159"
  Angle = 360
  Height = 4
  Placement = pos=(37,37.75,5.5) rot=(1,0,0;1.5708rad)
  Radius = 4
FEATURE [Part::Box] Box566  label="Cube757"
  Height = 16.5
  Length = 6
  Placement = pos=(34,33.75,-11) rot=(0,0,1;0rad)
  Width = 4
FEATURE [Part::MultiFuse] Fusion611
  Placement = pos=(0,-5,0) rot=(0,0,1;0rad)
  Shapes = -> [Cylinder974,Box566,Cylinder973,Box565,Cylinder980]
FEATURE [Part::Cylinder] Cylinder981  label="Cylinder1160"
  Angle = 360
  Height = 4
  Placement = pos=(37,32.75,5.5) rot=(1,0,0;1.5708rad)
  Radius = 1.25
FEATURE [Part::MultiFuse] Fusion612
  Shapes = -> [Cylinder976,Cylinder975,Cylinder979,Cylinder977,Cylinder981]
FEATURE [Part::MultiFuse] Fusion613
  Shapes = -> [Fusion611,Cylinder978]
FEATURE [Part::Cut] Cut702
  Base = -> Fusion613
  Tool = -> Fusion612
FEATURE [Part::Cut] Cut703
  Base = -> Fusion609
  Tool = -> Fusion607
FEATURE [Part::Chamfer] Chamfer105  label="front-axle-steering-arm"
  Base = -> Cut703
  Edges = 1 edges r=0.999: [Edge7]
FEATURE [Part::Chamfer] Chamfer106  label="front-axle-steering-arm-with-rear-link"
  Base = -> Cut702
  Edges = 1 edges r=0.999: [Edge7]
